annotation { "Feature Type Name" : "Feature", "Feature Type Description" : "" }
export const myFeature = defineFeature(function(context is Context, id is Id, definition is map)
    precondition{}
    {
        {
            var Q0;
            Q0=qCreatedBy(makeId("Top.planeOp"),FACE);
            var sketch = newSketch(context, id + "F0", { "sketchPlane" : qUnion([Q0])});
            skLineSegment(sketch, "E0.bottom", {"start": v(-40.55, -23.12) * mm, "end": v(-42.05, -23.12) * mm});
            skLineSegment(sketch, "E0.top", {"start": v(-40.55, 23.88) * mm, "end": v(-42.05, 23.88) * mm});
            skLineSegment(sketch, "E0.left", {"start": v(-40.55, -23.12) * mm, "end": v(-40.55, 23.88) * mm});
            skLineSegment(sketch, "E0.right", {"start": v(-42.05, -23.12) * mm, "end": v(-42.05, 23.88) * mm});
            skLineSegment(sketch, "E1.bottom", {"start": v(40.45, -23.12) * mm, "end": v(41.95, -23.12) * mm});
            skLineSegment(sketch, "E1.top", {"start": v(40.45, 23.88) * mm, "end": v(41.95, 23.88) * mm});
            skLineSegment(sketch, "E1.left", {"start": v(40.45, -23.12) * mm, "end": v(40.45, 23.88) * mm});
            skLineSegment(sketch, "E1.right", {"start": v(41.95, -23.12) * mm, "end": v(41.95, 23.88) * mm});
            skLineSegment(sketch, "E2.bottom", {"start": v(41.95, 23.88) * mm, "end": v(-42.05, 23.88) * mm});
            skLineSegment(sketch, "E2.top", {"start": v(41.95, 25.38) * mm, "end": v(-42.05, 25.38) * mm});
            skLineSegment(sketch, "E2.left", {"start": v(41.95, 23.88) * mm, "end": v(41.95, 25.38) * mm});
            skLineSegment(sketch, "E2.right", {"start": v(-42.05, 23.88) * mm, "end": v(-42.05, 25.38) * mm});
            skLineSegment(sketch, "E3.bottom", {"start": v(-40.55, -14.22) * mm, "end": v(-35.55, -14.22) * mm});
            skLineSegment(sketch, "E3.top", {"start": v(-40.55, -15.72) * mm, "end": v(-35.55, -15.72) * mm});
            skLineSegment(sketch, "E3.left", {"start": v(-40.55, -14.22) * mm, "end": v(-40.55, -15.72) * mm});
            skLineSegment(sketch, "E3.right", {"start": v(-35.55, -14.22) * mm, "end": v(-35.55, -15.72) * mm});
            skLineSegment(sketch, "E4.bottom", {"start": v(35.45, -15.72) * mm, "end": v(40.45, -15.72) * mm});
            skLineSegment(sketch, "E4.top", {"start": v(35.45, -14.22) * mm, "end": v(40.45, -14.22) * mm});
            skLineSegment(sketch, "E4.left", {"start": v(35.45, -15.72) * mm, "end": v(35.45, -14.22) * mm});
            skLineSegment(sketch, "E4.right", {"start": v(40.45, -15.72) * mm, "end": v(40.45, -14.22) * mm});
            skLineSegment(sketch, "E5.bottom", {"start": v(-41.7, -22.32) * mm, "end": v(-40.9, -22.32) * mm});
            skLineSegment(sketch, "E5.top", {"start": v(-41.7, -18.82) * mm, "end": v(-40.9, -18.82) * mm});
            skLineSegment(sketch, "E5.left", {"start": v(-41.7, -22.32) * mm, "end": v(-41.7, -18.82) * mm});
            skLineSegment(sketch, "E5.right", {"start": v(-40.9, -22.32) * mm, "end": v(-40.9, -18.82) * mm});
            skLineSegment(sketch, "E6.bottom", {"start": v(-41.7, 24.58) * mm, "end": v(-40.9, 24.58) * mm});
            skLineSegment(sketch, "E6.top", {"start": v(-41.7, 21.08) * mm, "end": v(-40.9, 21.08) * mm});
            skLineSegment(sketch, "E6.left", {"start": v(-41.7, 24.58) * mm, "end": v(-41.7, 21.08) * mm});
            skLineSegment(sketch, "E6.right", {"start": v(-40.9, 24.58) * mm, "end": v(-40.9, 21.08) * mm});
            skLineSegment(sketch, "E7.bottom", {"start": v(40.8, 24.58) * mm, "end": v(41.6, 24.58) * mm});
            skLineSegment(sketch, "E7.top", {"start": v(40.8, 21.08) * mm, "end": v(41.6, 21.08) * mm});
            skLineSegment(sketch, "E7.left", {"start": v(40.8, 24.58) * mm, "end": v(40.8, 21.08) * mm});
            skLineSegment(sketch, "E7.right", {"start": v(41.6, 24.58) * mm, "end": v(41.6, 21.08) * mm});
            skLineSegment(sketch, "E8.bottom", {"start": v(40.8, -18.82) * mm, "end": v(41.6, -18.82) * mm});
            skLineSegment(sketch, "E8.top", {"start": v(40.8, -22.32) * mm, "end": v(41.6, -22.32) * mm});
            skLineSegment(sketch, "E8.left", {"start": v(40.8, -18.82) * mm, "end": v(40.8, -22.32) * mm});
            skLineSegment(sketch, "E8.right", {"start": v(41.6, -18.82) * mm, "end": v(41.6, -22.32) * mm});
            skLineSegment(sketch, "E9.bottom", {"start": v(-41.6, -18.92) * mm, "end": v(-41, -18.92) * mm});
            skLineSegment(sketch, "E9.top", {"start": v(-41.6, -22.22) * mm, "end": v(-41, -22.22) * mm});
            skLineSegment(sketch, "E9.left", {"start": v(-41.6, -18.92) * mm, "end": v(-41.6, -22.22) * mm});
            skLineSegment(sketch, "E9.right", {"start": v(-41, -18.92) * mm, "end": v(-41, -22.22) * mm});
            skLineSegment(sketch, "E10.bottom", {"start": v(-41.6, 24.48) * mm, "end": v(-41, 24.48) * mm});
            skLineSegment(sketch, "E10.top", {"start": v(-41.6, 21.18) * mm, "end": v(-41, 21.18) * mm});
            skLineSegment(sketch, "E10.left", {"start": v(-41.6, 24.48) * mm, "end": v(-41.6, 21.18) * mm});
            skLineSegment(sketch, "E10.right", {"start": v(-41, 24.48) * mm, "end": v(-41, 21.18) * mm});
            skLineSegment(sketch, "E11.bottom", {"start": v(40.9, 24.48) * mm, "end": v(41.5, 24.48) * mm});
            skLineSegment(sketch, "E11.top", {"start": v(40.9, 21.18) * mm, "end": v(41.5, 21.18) * mm});
            skLineSegment(sketch, "E11.left", {"start": v(40.9, 24.48) * mm, "end": v(40.9, 21.18) * mm});
            skLineSegment(sketch, "E11.right", {"start": v(41.5, 24.48) * mm, "end": v(41.5, 21.18) * mm});
            skLineSegment(sketch, "E12.bottom", {"start": v(40.9, -18.92) * mm, "end": v(41.5, -18.92) * mm});
            skLineSegment(sketch, "E12.top", {"start": v(40.9, -22.22) * mm, "end": v(41.5, -22.22) * mm});
            skLineSegment(sketch, "E12.left", {"start": v(40.9, -18.92) * mm, "end": v(40.9, -22.22) * mm});
            skLineSegment(sketch, "E12.right", {"start": v(41.5, -18.92) * mm, "end": v(41.5, -22.22) * mm});
            skSolve(sketch);
        }
        {
            var Q0;
            Q0=makeQuery(id+"F0.imprint","IMPRINT",FACE,{"disambiguationData":[TD([[makeQuery(id+"F0.imprint","IMPRINT",EDGE,{"derivedFrom":sQuery(id+"F0.wireOp",EDGE,"E3.bottom")}),-1.0]])]});
            var Q1;
            {var subQ5=sQuery(id+"F0.wireOp",EDGE,"E0.bottom");Q1=makeQuery(id+"F0.imprint","IMPRINT",FACE,{"disambiguationData":[TD([[makeQuery(id+"F0.imprint","IMPRINT",EDGE,{"derivedFrom":subQ5}),-1.0]])]});}
            var Q2;
            Q2=makeQuery(id+"F0.imprint","IMPRINT",FACE,{"disambiguationData":[TD([[makeQuery(id+"F0.imprint","IMPRINT",EDGE,{"derivedFrom":sQuery(id+"F0.wireOp",EDGE,"E2.top")}),1.0]])]});
            var Q3;
            {var subQ5=sQuery(id+"F0.wireOp",EDGE,"E1.bottom");Q3=makeQuery(id+"F0.imprint","IMPRINT",FACE,{"disambiguationData":[TD([[makeQuery(id+"F0.imprint","IMPRINT",EDGE,{"derivedFrom":subQ5}),1.0]])]});}
            var Q4;
            Q4=makeQuery(id+"F0.imprint","IMPRINT",FACE,{"disambiguationData":[TD([[makeQuery(id+"F0.imprint","IMPRINT",EDGE,{"derivedFrom":sQuery(id+"F0.wireOp",EDGE,"E4.bottom")}),1.0]])]});
            var Q5;
            Q5=makeQuery(id+"F0.imprint","IMPRINT",FACE,{"disambiguationData":[TD([[makeQuery(id+"F0.imprint","IMPRINT",EDGE,{"derivedFrom":sQuery(id+"F0.wireOp",EDGE,"E5.bottom")}),1.0]])]});
            var Q6;
            Q6=makeQuery(id+"F0.imprint","IMPRINT",FACE,{"disambiguationData":[TD([[makeQuery(id+"F0.imprint","IMPRINT",EDGE,{"derivedFrom":sQuery(id+"F0.wireOp",EDGE,"E8.bottom")}),-1.0]])]});
            var Q7;
            {var subQ5=sQuery(id+"F0.wireOp",EDGE,"E7.top");Q7=makeQuery(id+"F0.imprint","IMPRINT",FACE,{"disambiguationData":[TD([[makeQuery(id+"F0.imprint","IMPRINT",EDGE,{"derivedFrom":subQ5}),1.0]])]});}
            var Q8;
            {var subQ5=sQuery(id+"F0.wireOp",EDGE,"E7.bottom");Q8=makeQuery(id+"F0.imprint","IMPRINT",FACE,{"disambiguationData":[TD([[makeQuery(id+"F0.imprint","IMPRINT",EDGE,{"derivedFrom":subQ5}),-1.0]])]});}
            var Q9;
            {var subQ5=sQuery(id+"F0.wireOp",EDGE,"E6.bottom");Q9=makeQuery(id+"F0.imprint","IMPRINT",FACE,{"disambiguationData":[TD([[makeQuery(id+"F0.imprint","IMPRINT",EDGE,{"derivedFrom":subQ5}),-1.0]])]});}
            var Q10;
            {var subQ5=sQuery(id+"F0.wireOp",EDGE,"E6.top");Q10=makeQuery(id+"F0.imprint","IMPRINT",FACE,{"disambiguationData":[TD([[makeQuery(id+"F0.imprint","IMPRINT",EDGE,{"derivedFrom":subQ5}),1.0]])]});}
            var Q11;
            Q11=makeQuery(id+"F0.imprint","IMPRINT",FACE,{"disambiguationData":[TD([[makeQuery(id+"F0.imprint","IMPRINT",EDGE,{"derivedFrom":sQuery(id+"F0.wireOp",EDGE,"E9.bottom")}),-1.0]])]});
            var Q12;
            {var subQ5=sQuery(id+"F0.wireOp",EDGE,"E10.top");Q12=makeQuery(id+"F0.imprint","IMPRINT",FACE,{"disambiguationData":[TD([[makeQuery(id+"F0.imprint","IMPRINT",EDGE,{"derivedFrom":subQ5}),1.0]])]});}
            var Q13;
            Q13=makeQuery(id+"F0.imprint","IMPRINT",FACE,{"disambiguationData":[TD([[makeQuery(id+"F0.imprint","IMPRINT",EDGE,{"derivedFrom":sQuery(id+"F0.wireOp",EDGE,"E12.bottom")}),-1.0]])]});
            var Q14;
            {var subQ5=sQuery(id+"F0.wireOp",EDGE,"E11.top");Q14=makeQuery(id+"F0.imprint","IMPRINT",FACE,{"disambiguationData":[TD([[makeQuery(id+"F0.imprint","IMPRINT",EDGE,{"derivedFrom":subQ5}),1.0]])]});}
            var Q15;
            {var subQ5=sQuery(id+"F0.wireOp",EDGE,"E11.bottom");Q15=makeQuery(id+"F0.imprint","IMPRINT",FACE,{"disambiguationData":[TD([[makeQuery(id+"F0.imprint","IMPRINT",EDGE,{"derivedFrom":subQ5}),-1.0]])]});}
            var Q16;
            {var subQ5=sQuery(id+"F0.wireOp",EDGE,"E10.bottom");Q16=makeQuery(id+"F0.imprint","IMPRINT",FACE,{"disambiguationData":[TD([[makeQuery(id+"F0.imprint","IMPRINT",EDGE,{"derivedFrom":subQ5}),-1.0]])]});}
            extrude(context, id + "F1", {"entities" : qUnion([Q0, Q1, Q2, Q3, Q4, Q5, Q6, Q7, Q8, Q9, Q10, Q11, Q12, Q13, Q14, Q15, Q16]), "depth" : 120 * mm, "offsetDistance" : 25 * mm, "hasSecondDirection" : true, "secondDirectionOppositeDirection" : true, "secondDirectionDepth" : 1.5 * mm});
        }
        {
            var Q0;
            Q0=makeQuery(id+"F1.opExtrude","SWEPT_FACE",FACE,{"disambiguationData":[OSD([sQuery(id+"F0.wireOp",EDGE,"E3.top")])]});
            var sketch = newSketch(context, id + "F2", { "sketchPlane" : qUnion([Q0])});
            skPoint(sketch, "E13", {"position": v(-37.51, 4) * mm});
            skPoint(sketch, "E14", {"position": v(-37.51, 2) * mm});
            skPoint(sketch, "E15", {"position": v(-37.48, 11.5) * mm});
            skPoint(sketch, "E16", {"position": v(-37.51, 9.5) * mm});
            skPoint(sketch, "E17", {"position": v(-37.48, 19) * mm});
            skPoint(sketch, "E18", {"position": v(-37.48, 17) * mm});
            skPoint(sketch, "E19", {"position": v(-37.44, 26.5) * mm});
            skPoint(sketch, "E20", {"position": v(-37.44, 24.5) * mm});
            skPoint(sketch, "E21", {"position": v(-37.44, 34) * mm});
            skPoint(sketch, "E22", {"position": v(-37.44, 32) * mm});
            skPoint(sketch, "E23", {"position": v(-37.4, 41.5) * mm});
            skPoint(sketch, "E24", {"position": v(-37.4, 39.5) * mm});
            skPoint(sketch, "E25", {"position": v(-37.4, 49) * mm});
            skPoint(sketch, "E26", {"position": v(-37.4, 47) * mm});
            skPoint(sketch, "E27", {"position": v(-37.37, 56.5) * mm});
            skPoint(sketch, "E28", {"position": v(-37.37, 54.5) * mm});
            skPoint(sketch, "E29", {"position": v(-37.37, 64) * mm});
            skPoint(sketch, "E30", {"position": v(-37.37, 62) * mm});
            skPoint(sketch, "E31", {"position": v(-37.33, 71.5) * mm});
            skPoint(sketch, "E32", {"position": v(-37.37, 69.5) * mm});
            skPoint(sketch, "E33", {"position": v(-37.33, 79) * mm});
            skPoint(sketch, "E34", {"position": v(-37.33, 77) * mm});
            skPoint(sketch, "E35", {"position": v(-37.3, 86.5) * mm});
            skPoint(sketch, "E36", {"position": v(-37.3, 84.5) * mm});
            skPoint(sketch, "E37", {"position": v(-37.3, 94) * mm});
            skPoint(sketch, "E38", {"position": v(-37.3, 92) * mm});
            skPoint(sketch, "E39", {"position": v(-37.25, 101.5) * mm});
            skPoint(sketch, "E40", {"position": v(-37.25, 99.5) * mm});
            skPoint(sketch, "E41", {"position": v(-37.25, 109) * mm});
            skPoint(sketch, "E42", {"position": v(-37.25, 107) * mm});
            skPoint(sketch, "E43", {"position": v(-37.22, 116.5) * mm});
            skPoint(sketch, "E44", {"position": v(-37.22, 114.5) * mm});
            skSolve(sketch);
        }
        {
            var Q0;
            Q0=sQuery(id+"F2.wireOp",VERTEX,"E25");
            var Q1;
            Q1=sQuery(id+"F2.wireOp",VERTEX,"E26");
            var Q2;
            Q2=sQuery(id+"F2.wireOp",VERTEX,"E28");
            var Q3;
            Q3=sQuery(id+"F2.wireOp",VERTEX,"E27");
            var Q4;
            Q4=sQuery(id+"F2.wireOp",VERTEX,"E30");
            var Q5;
            Q5=sQuery(id+"F2.wireOp",VERTEX,"E29");
            var Q6;
            Q6=sQuery(id+"F2.wireOp",VERTEX,"E43");
            var Q7;
            Q7=sQuery(id+"F2.wireOp",VERTEX,"E44");
            var Q8;
            Q8=sQuery(id+"F2.wireOp",VERTEX,"E41");
            var Q9;
            Q9=sQuery(id+"F2.wireOp",VERTEX,"E42");
            var Q10;
            Q10=sQuery(id+"F2.wireOp",VERTEX,"E39");
            var Q11;
            Q11=sQuery(id+"F2.wireOp",VERTEX,"E40");
            var Q12;
            Q12=sQuery(id+"F2.wireOp",VERTEX,"E37");
            var Q13;
            Q13=sQuery(id+"F2.wireOp",VERTEX,"E38");
            var Q14;
            Q14=sQuery(id+"F2.wireOp",VERTEX,"E35");
            var Q15;
            Q15=sQuery(id+"F2.wireOp",VERTEX,"E36");
            var Q16;
            Q16=sQuery(id+"F2.wireOp",VERTEX,"E33");
            var Q17;
            Q17=sQuery(id+"F2.wireOp",VERTEX,"E34");
            var Q18;
            Q18=sQuery(id+"F2.wireOp",VERTEX,"E31");
            var Q19;
            Q19=sQuery(id+"F2.wireOp",VERTEX,"E32");
            var Q20;
            Q20=sQuery(id+"F2.wireOp",VERTEX,"E23");
            var Q21;
            Q21=sQuery(id+"F2.wireOp",VERTEX,"E24");
            var Q22;
            Q22=sQuery(id+"F2.wireOp",VERTEX,"E21");
            var Q23;
            Q23=sQuery(id+"F2.wireOp",VERTEX,"E22");
            var Q24;
            Q24=sQuery(id+"F2.wireOp",VERTEX,"E19");
            var Q25;
            Q25=sQuery(id+"F2.wireOp",VERTEX,"E20");
            var Q26;
            Q26=sQuery(id+"F2.wireOp",VERTEX,"E17");
            var Q27;
            Q27=sQuery(id+"F2.wireOp",VERTEX,"E18");
            var Q28;
            Q28=sQuery(id+"F2.wireOp",VERTEX,"E15");
            var Q29;
            Q29=sQuery(id+"F2.wireOp",VERTEX,"E16");
            var Q30;
            Q30=sQuery(id+"F2.wireOp",VERTEX,"E13");
            var Q31;
            Q31=sQuery(id+"F2.wireOp",VERTEX,"E14");
            var Q32;
            Q32=makeQuery(id+"F1.opExtrude","SWEPT_BODY",BODY,{"disambiguationData":[OSD([sQuery(id+"F0.wireOp",EDGE,"E0.bottom"),sQuery(id+"F0.wireOp",EDGE,"E0.left"),sQuery(id+"F0.wireOp",EDGE,"E0.right"),sQuery(id+"F0.wireOp",EDGE,"E1.bottom"),sQuery(id+"F0.wireOp",EDGE,"E1.left"),sQuery(id+"F0.wireOp",EDGE,"E1.right"),sQuery(id+"F0.wireOp",EDGE,"E2.bottom"),sQuery(id+"F0.wireOp",EDGE,"E2.top"),sQuery(id+"F0.wireOp",EDGE,"E2.left"),sQuery(id+"F0.wireOp",EDGE,"E2.right"),sQuery(id+"F0.wireOp",EDGE,"E3.bottom"),sQuery(id+"F0.wireOp",EDGE,"E3.top"),sQuery(id+"F0.wireOp",EDGE,"E3.right"),sQuery(id+"F0.wireOp",EDGE,"E4.bottom"),sQuery(id+"F0.wireOp",EDGE,"E4.top"),sQuery(id+"F0.wireOp",EDGE,"E4.left")])]});
            hole(context, id + "F3", {"style" : HoleStyle.SIMPLE, "endStyle" : HoleEndStyle.BLIND, "holeDiameter" : .8 * mm, "majorDiameter" : 5 * mm, "holeDepth" : 2 * mm, "isTappedThrough" : true, "tappedDepth" : 12 * mm, "tapClearance" : 3, "locations" : qUnion([Q0, Q1, Q2, Q3, Q4, Q5, Q6, Q7, Q8, Q9, Q10, Q11, Q12, Q13, Q14, Q15, Q16, Q17, Q18, Q19, Q20, Q21, Q22, Q23, Q24, Q25, Q26, Q27, Q28, Q29, Q30, Q31]), "scope" : qUnion([Q32])});
        }
        {
            var Q0;
            Q0=makeQuery(id+"F1.opExtrude","SWEPT_FACE",FACE,{"disambiguationData":[OSD([sQuery(id+"F0.wireOp",EDGE,"E4.bottom")])]});
            var sketch = newSketch(context, id + "F4", { "sketchPlane" : qUnion([Q0])});
            skPoint(sketch, "E45", {"position": v(37.47, 4) * mm});
            skPoint(sketch, "E46", {"position": v(37.47, 2) * mm});
            skPoint(sketch, "E47", {"position": v(37.52, 11.5) * mm});
            skPoint(sketch, "E48", {"position": v(37.47, 9.5) * mm});
            skPoint(sketch, "E49", {"position": v(37.52, 19) * mm});
            skPoint(sketch, "E50", {"position": v(37.52, 17) * mm});
            skPoint(sketch, "E51", {"position": v(37.56, 26.5) * mm});
            skPoint(sketch, "E52", {"position": v(37.56, 24.5) * mm});
            skPoint(sketch, "E53", {"position": v(37.56, 34) * mm});
            skPoint(sketch, "E54", {"position": v(37.56, 32) * mm});
            skPoint(sketch, "E55", {"position": v(37.6, 41.5) * mm});
            skPoint(sketch, "E56", {"position": v(37.6, 39.5) * mm});
            skPoint(sketch, "E57", {"position": v(37.6, 49) * mm});
            skPoint(sketch, "E58", {"position": v(37.6, 47) * mm});
            skPoint(sketch, "E59", {"position": v(37.63, 56.5) * mm});
            skPoint(sketch, "E60", {"position": v(37.63, 54.5) * mm});
            skPoint(sketch, "E61", {"position": v(37.63, 64) * mm});
            skPoint(sketch, "E62", {"position": v(37.63, 62) * mm});
            skPoint(sketch, "E63", {"position": v(37.67, 71.5) * mm});
            skPoint(sketch, "E64", {"position": v(37.63, 69.5) * mm});
            skPoint(sketch, "E65", {"position": v(37.67, 79) * mm});
            skPoint(sketch, "E66", {"position": v(37.67, 77) * mm});
            skPoint(sketch, "E67", {"position": v(37.7, 86.5) * mm});
            skPoint(sketch, "E68", {"position": v(37.7, 84.5) * mm});
            skPoint(sketch, "E69", {"position": v(37.7, 94) * mm});
            skPoint(sketch, "E70", {"position": v(37.7, 92) * mm});
            skPoint(sketch, "E71", {"position": v(37.74, 101.5) * mm});
            skPoint(sketch, "E72", {"position": v(37.74, 99.5) * mm});
            skPoint(sketch, "E73", {"position": v(37.74, 109) * mm});
            skPoint(sketch, "E74", {"position": v(37.74, 107) * mm});
            skPoint(sketch, "E75", {"position": v(37.78, 116.5) * mm});
            skPoint(sketch, "E76", {"position": v(37.78, 114.5) * mm});
            skSolve(sketch);
        }
        {
            var Q0;
            Q0=sQuery(id+"F4.wireOp",VERTEX,"E75");
            var Q1;
            Q1=sQuery(id+"F4.wireOp",VERTEX,"E76");
            var Q2;
            Q2=sQuery(id+"F4.wireOp",VERTEX,"E73");
            var Q3;
            Q3=sQuery(id+"F4.wireOp",VERTEX,"E74");
            var Q4;
            Q4=sQuery(id+"F4.wireOp",VERTEX,"E71");
            var Q5;
            Q5=sQuery(id+"F4.wireOp",VERTEX,"E72");
            var Q6;
            Q6=sQuery(id+"F4.wireOp",VERTEX,"E70");
            var Q7;
            Q7=sQuery(id+"F4.wireOp",VERTEX,"E69");
            var Q8;
            Q8=sQuery(id+"F4.wireOp",VERTEX,"E67");
            var Q9;
            Q9=sQuery(id+"F4.wireOp",VERTEX,"E68");
            var Q10;
            Q10=sQuery(id+"F4.wireOp",VERTEX,"E65");
            var Q11;
            Q11=sQuery(id+"F4.wireOp",VERTEX,"E66");
            var Q12;
            Q12=sQuery(id+"F4.wireOp",VERTEX,"E63");
            var Q13;
            Q13=sQuery(id+"F4.wireOp",VERTEX,"E64");
            var Q14;
            Q14=sQuery(id+"F4.wireOp",VERTEX,"E61");
            var Q15;
            Q15=sQuery(id+"F4.wireOp",VERTEX,"E62");
            var Q16;
            Q16=sQuery(id+"F4.wireOp",VERTEX,"E59");
            var Q17;
            Q17=sQuery(id+"F4.wireOp",VERTEX,"E60");
            var Q18;
            Q18=sQuery(id+"F4.wireOp",VERTEX,"E57");
            var Q19;
            Q19=sQuery(id+"F4.wireOp",VERTEX,"E58");
            var Q20;
            Q20=sQuery(id+"F4.wireOp",VERTEX,"E55");
            var Q21;
            Q21=sQuery(id+"F4.wireOp",VERTEX,"E56");
            var Q22;
            Q22=sQuery(id+"F4.wireOp",VERTEX,"E53");
            var Q23;
            Q23=sQuery(id+"F4.wireOp",VERTEX,"E54");
            var Q24;
            Q24=sQuery(id+"F4.wireOp",VERTEX,"E51");
            var Q25;
            Q25=sQuery(id+"F4.wireOp",VERTEX,"E52");
            var Q26;
            Q26=sQuery(id+"F4.wireOp",VERTEX,"E49");
            var Q27;
            Q27=sQuery(id+"F4.wireOp",VERTEX,"E50");
            var Q28;
            Q28=sQuery(id+"F4.wireOp",VERTEX,"E47");
            var Q29;
            Q29=sQuery(id+"F4.wireOp",VERTEX,"E48");
            var Q30;
            Q30=sQuery(id+"F4.wireOp",VERTEX,"E45");
            var Q31;
            Q31=sQuery(id+"F4.wireOp",VERTEX,"E46");
            var Q32;
            Q32=makeQuery(id+"F1.opExtrude","SWEPT_BODY",BODY,{"disambiguationData":[OSD([sQuery(id+"F0.wireOp",EDGE,"E0.bottom"),sQuery(id+"F0.wireOp",EDGE,"E0.left"),sQuery(id+"F0.wireOp",EDGE,"E0.right"),sQuery(id+"F0.wireOp",EDGE,"E1.bottom"),sQuery(id+"F0.wireOp",EDGE,"E1.left"),sQuery(id+"F0.wireOp",EDGE,"E1.right"),sQuery(id+"F0.wireOp",EDGE,"E2.bottom"),sQuery(id+"F0.wireOp",EDGE,"E2.top"),sQuery(id+"F0.wireOp",EDGE,"E2.left"),sQuery(id+"F0.wireOp",EDGE,"E2.right"),sQuery(id+"F0.wireOp",EDGE,"E3.bottom"),sQuery(id+"F0.wireOp",EDGE,"E3.top"),sQuery(id+"F0.wireOp",EDGE,"E3.right"),sQuery(id+"F0.wireOp",EDGE,"E4.bottom"),sQuery(id+"F0.wireOp",EDGE,"E4.top"),sQuery(id+"F0.wireOp",EDGE,"E4.left")])]});
            hole(context, id + "F5", {"style" : HoleStyle.SIMPLE, "endStyle" : HoleEndStyle.BLIND, "holeDiameter" : .8 * mm, "majorDiameter" : 5 * mm, "holeDepth" : 2 * mm, "isTappedThrough" : true, "tappedDepth" : 12 * mm, "tapClearance" : 3, "locations" : qUnion([Q0, Q1, Q2, Q3, Q4, Q5, Q6, Q7, Q8, Q9, Q10, Q11, Q12, Q13, Q14, Q15, Q16, Q17, Q18, Q19, Q20, Q21, Q22, Q23, Q24, Q25, Q26, Q27, Q28, Q29, Q30, Q31]), "scope" : qUnion([Q32])});
        }
        {
            var Q0;
            {var subQ5=sQuery(id+"F0.wireOp",EDGE,"E10.top");Q0=makeQuery(id+"F0.imprint","IMPRINT",FACE,{"disambiguationData":[TD([[makeQuery(id+"F0.imprint","IMPRINT",EDGE,{"derivedFrom":subQ5}),1.0]])]});}
            var Q1;
            {var subQ5=sQuery(id+"F0.wireOp",EDGE,"E10.bottom");Q1=makeQuery(id+"F0.imprint","IMPRINT",FACE,{"disambiguationData":[TD([[makeQuery(id+"F0.imprint","IMPRINT",EDGE,{"derivedFrom":subQ5}),-1.0]])]});}
            var Q2;
            Q2=makeQuery(id+"F0.imprint","IMPRINT",FACE,{"disambiguationData":[TD([[makeQuery(id+"F0.imprint","IMPRINT",EDGE,{"derivedFrom":sQuery(id+"F0.wireOp",EDGE,"E9.bottom")}),-1.0]])]});
            var Q3;
            {var subQ5=sQuery(id+"F0.wireOp",EDGE,"E11.top");Q3=makeQuery(id+"F0.imprint","IMPRINT",FACE,{"disambiguationData":[TD([[makeQuery(id+"F0.imprint","IMPRINT",EDGE,{"derivedFrom":subQ5}),1.0]])]});}
            var Q4;
            {var subQ5=sQuery(id+"F0.wireOp",EDGE,"E11.bottom");Q4=makeQuery(id+"F0.imprint","IMPRINT",FACE,{"disambiguationData":[TD([[makeQuery(id+"F0.imprint","IMPRINT",EDGE,{"derivedFrom":subQ5}),-1.0]])]});}
            var Q5;
            Q5=makeQuery(id+"F0.imprint","IMPRINT",FACE,{"disambiguationData":[TD([[makeQuery(id+"F0.imprint","IMPRINT",EDGE,{"derivedFrom":sQuery(id+"F0.wireOp",EDGE,"E12.bottom")}),-1.0]])]});
            extrude(context, id + "F6", {"entities" : qUnion([Q0, Q1, Q2, Q3, Q4, Q5]), "oppositeDirection" : true, "depth" : 2.8 * mm, "offsetDistance" : 25 * mm});
        }
        {
            var Q0;
            Q0=makeQuery(id+"F0.imprint","IMPRINT",FACE,{"disambiguationData":[TD([[makeQuery(id+"F0.imprint","IMPRINT",EDGE,{"derivedFrom":sQuery(id+"F0.wireOp",EDGE,"E5.bottom")}),1.0]])]});
            var Q1;
            {var subQ5=sQuery(id+"F0.wireOp",EDGE,"E7.bottom");Q1=makeQuery(id+"F0.imprint","IMPRINT",FACE,{"disambiguationData":[TD([[makeQuery(id+"F0.imprint","IMPRINT",EDGE,{"derivedFrom":subQ5}),-1.0]])]});}
            var Q2;
            {var subQ5=sQuery(id+"F0.wireOp",EDGE,"E10.top");Q2=makeQuery(id+"F0.imprint","IMPRINT",FACE,{"disambiguationData":[TD([[makeQuery(id+"F0.imprint","IMPRINT",EDGE,{"derivedFrom":subQ5}),1.0]])]});}
            var Q3;
            {var subQ1=sQuery(id+"F0.wireOp",EDGE,"E6.top");Q3=makeQuery(id+"F0.imprint","IMPRINT",FACE,{"disambiguationData":[TD([[makeQuery(id+"F0.imprint","IMPRINT",EDGE,{"derivedFrom":subQ1}),1.0]])]});}
            var Q4;
            {var subQ5=sQuery(id+"F0.wireOp",EDGE,"E10.bottom");Q4=makeQuery(id+"F0.imprint","IMPRINT",FACE,{"disambiguationData":[TD([[makeQuery(id+"F0.imprint","IMPRINT",EDGE,{"derivedFrom":subQ5}),-1.0]])]});}
            var Q5;
            {var subQ1=sQuery(id+"F0.wireOp",EDGE,"E6.bottom");Q5=makeQuery(id+"F0.imprint","IMPRINT",FACE,{"disambiguationData":[TD([[makeQuery(id+"F0.imprint","IMPRINT",EDGE,{"derivedFrom":subQ1}),-1.0]])]});}
            var Q6;
            Q6=makeQuery(id+"F0.imprint","IMPRINT",FACE,{"disambiguationData":[TD([[makeQuery(id+"F0.imprint","IMPRINT",EDGE,{"derivedFrom":sQuery(id+"F0.wireOp",EDGE,"E9.bottom")}),-1.0]])]});
            var Q7;
            Q7=makeQuery(id+"F0.imprint","IMPRINT",FACE,{"disambiguationData":[TD([[makeQuery(id+"F0.imprint","IMPRINT",EDGE,{"derivedFrom":sQuery(id+"F0.wireOp",EDGE,"E12.bottom")}),-1.0]])]});
            var Q8;
            Q8=makeQuery(id+"F0.imprint","IMPRINT",FACE,{"disambiguationData":[TD([[makeQuery(id+"F0.imprint","IMPRINT",EDGE,{"derivedFrom":sQuery(id+"F0.wireOp",EDGE,"E8.bottom")}),-1.0]])]});
            var Q9;
            {var subQ1=sQuery(id+"F0.wireOp",EDGE,"E7.top");Q9=makeQuery(id+"F0.imprint","IMPRINT",FACE,{"disambiguationData":[TD([[makeQuery(id+"F0.imprint","IMPRINT",EDGE,{"derivedFrom":subQ1}),1.0]])]});}
            var Q10;
            {var subQ5=sQuery(id+"F0.wireOp",EDGE,"E11.top");Q10=makeQuery(id+"F0.imprint","IMPRINT",FACE,{"disambiguationData":[TD([[makeQuery(id+"F0.imprint","IMPRINT",EDGE,{"derivedFrom":subQ5}),1.0]])]});}
            var Q11;
            {var subQ5=sQuery(id+"F0.wireOp",EDGE,"E11.bottom");Q11=makeQuery(id+"F0.imprint","IMPRINT",FACE,{"disambiguationData":[TD([[makeQuery(id+"F0.imprint","IMPRINT",EDGE,{"derivedFrom":subQ5}),-1.0]])]});}
            extrude(context, id + "F7", {"entities" : qUnion([Q0, Q1, Q2, Q3, Q4, Q5, Q6, Q7, Q8, Q9, Q10, Q11]), "operationType" : NewBodyOperationType.REMOVE, "depth" : 120 * mm, "offsetDistance" : 25 * mm, "hasSecondDirection" : true, "secondDirectionOppositeDirection" : false, "secondDirectionDepth" : 118.5 * mm});
        }
        {
            var Q0;
            Q0=makeQuery(id+"F1.opExtrude","SWEPT_FACE",FACE,{"disambiguationData":[OSD([sQuery(id+"F0.wireOp",EDGE,"E2.top")])]});
            var sketch = newSketch(context, id + "F8", { "sketchPlane" : qUnion([Q0])});
            skLineSegment(sketch, "E77.bottom", {"start": v(-29.95, -1.5) * mm, "end": v(30.05, -1.5) * mm});
            skLineSegment(sketch, "E77.top", {"start": v(-24.95, 8.5) * mm, "end": v(25.05, 8.5) * mm});
            skLineSegment(sketch, "E77.left", {"start": v(-29.95, -1.5) * mm, "end": v(-29.95, 3.5) * mm});
            skLineSegment(sketch, "E77.right", {"start": v(30.05, -1.5) * mm, "end": v(30.05, 3.5) * mm});
            skPoint(sketch, "E78.visualSharp", {"position": v(-29.95, 8.5) * mm});
            skArc(sketch, "E78.filletArc", {"start": v(-24.95, 8.5) * mm, "mid": v(-28.5, 7.04) * mm, "end": v(-29.95, 3.5) * mm});
            skPoint(sketch, "E79.visualSharp", {"position": v(30.05, 8.5) * mm});
            skArc(sketch, "E79.filletArc", {"start": v(30.05, 3.5) * mm, "mid": v(28.58, 7.04) * mm, "end": v(25.05, 8.5) * mm});
            skText(sketch, "E80", { "text": "Raspberry Pi Zero", "fontName": "OpenSans-Regular.ttf"});
            skText(sketch, "E81", { "text": "Mini Rack", "fontName": "OpenSans-Regular.ttf"});
            skText(sketch, "E82", { "text": "By Cyron Design", "fontName": "OpenSans-Regular.ttf"});
            skLineSegment(sketch, "E83", {"start": v(-41.95, 115.78) * mm, "end": v(42.05, 115.78) * mm});
            skPoint(sketch, "E84", {"position": v(0.05, 115.78) * mm});
            skLineSegment(sketch, "E85", {"start": v(-7.06, 71.95) * mm, "end": v(-7.1, 71.95) * mm});
            skLineSegment(sketch, "E86", {"start": v(-7.1, 71.95) * mm, "end": v(-7.32, 71.9) * mm});
            skLineSegment(sketch, "E87", {"start": v(-7.32, 71.9) * mm, "end": v(-7.55, 71.77) * mm});
            skLineSegment(sketch, "E88", {"start": v(-7.55, 71.77) * mm, "end": v(-7.6, 71.73) * mm});
            skLineSegment(sketch, "E89", {"start": v(-7.6, 71.73) * mm, "end": v(-7.68, 71.76) * mm});
            skLineSegment(sketch, "E90", {"start": v(-7.68, 71.76) * mm, "end": v(-7.96, 71.84) * mm});
            skLineSegment(sketch, "E91", {"start": v(-7.96, 71.84) * mm, "end": v(-8.3, 71.88) * mm});
            skLineSegment(sketch, "E92", {"start": v(-8.3, 71.88) * mm, "end": v(-8.64, 71.8) * mm});
            skLineSegment(sketch, "E93", {"start": v(-8.64, 71.8) * mm, "end": v(-8.9, 71.66) * mm});
            skLineSegment(sketch, "E94", {"start": v(-8.9, 71.66) * mm, "end": v(-8.97, 71.6) * mm});
            skLineSegment(sketch, "E95", {"start": v(-8.97, 71.6) * mm, "end": v(-9.07, 71.61) * mm});
            skLineSegment(sketch, "E96", {"start": v(-9.07, 71.61) * mm, "end": v(-9.38, 71.62) * mm});
            skLineSegment(sketch, "E97", {"start": v(-9.38, 71.62) * mm, "end": v(-9.66, 71.56) * mm});
            skLineSegment(sketch, "E98", {"start": v(-9.66, 71.56) * mm, "end": v(-9.85, 71.45) * mm});
            skLineSegment(sketch, "E99", {"start": v(-9.85, 71.45) * mm, "end": v(-9.95, 71.35) * mm});
            skLineSegment(sketch, "E100", {"start": v(-9.95, 71.35) * mm, "end": v(-9.98, 71.3) * mm});
            skLineSegment(sketch, "E101", {"start": v(-9.98, 71.3) * mm, "end": v(-10, 71.3) * mm});
            skLineSegment(sketch, "E102", {"start": v(-10, 71.3) * mm, "end": v(-10.07, 71.31) * mm});
            skLineSegment(sketch, "E103", {"start": v(-10.07, 71.31) * mm, "end": v(-10.22, 71.32) * mm});
            skLineSegment(sketch, "E104", {"start": v(-10.22, 71.32) * mm, "end": v(-10.4, 71.32) * mm});
            skLineSegment(sketch, "E105", {"start": v(-10.4, 71.32) * mm, "end": v(-10.62, 71.3) * mm});
            skLineSegment(sketch, "E106", {"start": v(-10.62, 71.3) * mm, "end": v(-10.85, 71.25) * mm});
            skLineSegment(sketch, "E107", {"start": v(-10.85, 71.25) * mm, "end": v(-11.08, 71.17) * mm});
            skLineSegment(sketch, "E108", {"start": v(-11.08, 71.17) * mm, "end": v(-11.29, 71.03) * mm});
            skLineSegment(sketch, "E109", {"start": v(-11.29, 71.03) * mm, "end": v(-11.43, 70.88) * mm});
            skLineSegment(sketch, "E110", {"start": v(-11.43, 70.88) * mm, "end": v(-11.47, 70.82) * mm});
            skLineSegment(sketch, "E111", {"start": v(-11.47, 70.82) * mm, "end": v(-11.56, 70.83) * mm});
            skLineSegment(sketch, "E112", {"start": v(-11.56, 70.83) * mm, "end": v(-11.83, 70.83) * mm});
            skLineSegment(sketch, "E113", {"start": v(-11.83, 70.83) * mm, "end": v(-12.13, 70.77) * mm});
            skLineSegment(sketch, "E114", {"start": v(-12.13, 70.77) * mm, "end": v(-12.36, 70.64) * mm});
            skLineSegment(sketch, "E115", {"start": v(-12.36, 70.64) * mm, "end": v(-12.52, 70.47) * mm});
            skLineSegment(sketch, "E116", {"start": v(-12.52, 70.47) * mm, "end": v(-12.6, 70.26) * mm});
            skLineSegment(sketch, "E117", {"start": v(-12.6, 70.26) * mm, "end": v(-12.64, 70.02) * mm});
            skLineSegment(sketch, "E118", {"start": v(-12.64, 70.02) * mm, "end": v(-12.6, 69.76) * mm});
            skLineSegment(sketch, "E119", {"start": v(-12.6, 69.76) * mm, "end": v(-12.52, 69.56) * mm});
            skLineSegment(sketch, "E120", {"start": v(-12.52, 69.56) * mm, "end": v(-12.48, 69.5) * mm});
            skLineSegment(sketch, "E121", {"start": v(-12.48, 69.5) * mm, "end": v(-12.53, 69.44) * mm});
            skLineSegment(sketch, "E122", {"start": v(-12.53, 69.44) * mm, "end": v(-12.64, 69.25) * mm});
            skLineSegment(sketch, "E123", {"start": v(-12.64, 69.25) * mm, "end": v(-12.72, 68.96) * mm});
            skLineSegment(sketch, "E124", {"start": v(-12.72, 68.96) * mm, "end": v(-12.67, 68.62) * mm});
            skLineSegment(sketch, "E125", {"start": v(-12.67, 68.62) * mm, "end": v(-12.5, 68.3) * mm});
            skLineSegment(sketch, "E126", {"start": v(-12.5, 68.3) * mm, "end": v(-12.42, 68.2) * mm});
            skLineSegment(sketch, "E127", {"start": v(-12.42, 68.2) * mm, "end": v(-12.45, 68.13) * mm});
            skLineSegment(sketch, "E128", {"start": v(-12.45, 68.13) * mm, "end": v(-12.5, 67.92) * mm});
            skLineSegment(sketch, "E129", {"start": v(-12.5, 67.92) * mm, "end": v(-12.47, 67.63) * mm});
            skLineSegment(sketch, "E130", {"start": v(-12.47, 67.63) * mm, "end": v(-12.32, 67.32) * mm});
            skLineSegment(sketch, "E131", {"start": v(-12.32, 67.32) * mm, "end": v(-12.14, 67.06) * mm});
            skLineSegment(sketch, "E132", {"start": v(-12.14, 67.06) * mm, "end": v(-12.07, 66.99) * mm});
            skLineSegment(sketch, "E133", {"start": v(-12.07, 66.99) * mm, "end": v(-12.08, 66.9) * mm});
            skLineSegment(sketch, "E134", {"start": v(-12.08, 66.9) * mm, "end": v(-12.09, 66.64) * mm});
            skLineSegment(sketch, "E135", {"start": v(-12.09, 66.64) * mm, "end": v(-12, 66.34) * mm});
            skLineSegment(sketch, "E136", {"start": v(-12, 66.34) * mm, "end": v(-11.82, 66.08) * mm});
            skLineSegment(sketch, "E137", {"start": v(-11.82, 66.08) * mm, "end": v(-11.63, 65.9) * mm});
            skLineSegment(sketch, "E138", {"start": v(-11.63, 65.9) * mm, "end": v(-11.56, 65.86) * mm});
            skLineSegment(sketch, "E139", {"start": v(-11.56, 65.86) * mm, "end": v(-11.58, 65.74) * mm});
            skLineSegment(sketch, "E140", {"start": v(-11.58, 65.74) * mm, "end": v(-11.5, 65.4) * mm});
            skLineSegment(sketch, "E141", {"start": v(-11.5, 65.4) * mm, "end": v(-11.25, 65.04) * mm});
            skLineSegment(sketch, "E142", {"start": v(-11.25, 65.04) * mm, "end": v(-10.96, 64.79) * mm});
            skLineSegment(sketch, "E143", {"start": v(-10.96, 64.79) * mm, "end": v(-10.78, 64.67) * mm});
            skLineSegment(sketch, "E144", {"start": v(-10.78, 64.67) * mm, "end": v(-10.73, 64.63) * mm});
            skLineSegment(sketch, "E145", {"start": v(-10.73, 64.63) * mm, "end": v(-10.71, 64.56) * mm});
            skLineSegment(sketch, "E146", {"start": v(-10.71, 64.56) * mm, "end": v(-10.64, 64.34) * mm});
            skLineSegment(sketch, "E147", {"start": v(-10.64, 64.34) * mm, "end": v(-10.47, 64.07) * mm});
            skLineSegment(sketch, "E148", {"start": v(-10.47, 64.07) * mm, "end": v(-10.17, 63.83) * mm});
            skLineSegment(sketch, "E149", {"start": v(-10.17, 63.83) * mm, "end": v(-9.8, 63.68) * mm});
            skLineSegment(sketch, "E150", {"start": v(-9.8, 63.68) * mm, "end": v(-9.68, 63.65) * mm});
            skLineSegment(sketch, "E151", {"start": v(-9.68, 63.65) * mm, "end": v(-9.66, 63.55) * mm});
            skLineSegment(sketch, "E152", {"start": v(-9.66, 63.55) * mm, "end": v(-9.52, 63.28) * mm});
            skLineSegment(sketch, "E153", {"start": v(-9.52, 63.28) * mm, "end": v(-9.26, 63.06) * mm});
            skLineSegment(sketch, "E154", {"start": v(-9.26, 63.06) * mm, "end": v(-8.94, 62.92) * mm});
            skLineSegment(sketch, "E155", {"start": v(-8.94, 62.92) * mm, "end": v(-8.68, 62.85) * mm});
            skLineSegment(sketch, "E156", {"start": v(-8.68, 62.85) * mm, "end": v(-8.6, 62.82) * mm});
            skLineSegment(sketch, "E157", {"start": v(-8.6, 62.82) * mm, "end": v(-8.74, 62.74) * mm});
            skLineSegment(sketch, "E158", {"start": v(-8.74, 62.74) * mm, "end": v(-9.16, 62.47) * mm});
            skLineSegment(sketch, "E159", {"start": v(-9.16, 62.47) * mm, "end": v(-9.7, 62.08) * mm});
            skLineSegment(sketch, "E160", {"start": v(-9.7, 62.08) * mm, "end": v(-10.18, 61.62) * mm});
            skLineSegment(sketch, "E161", {"start": v(-10.18, 61.62) * mm, "end": v(-10.6, 61.09) * mm});
            skLineSegment(sketch, "E162", {"start": v(-10.6, 61.09) * mm, "end": v(-10.96, 60.46) * mm});
            skLineSegment(sketch, "E163", {"start": v(-10.96, 60.46) * mm, "end": v(-11.23, 59.73) * mm});
            skLineSegment(sketch, "E164", {"start": v(-11.23, 59.73) * mm, "end": v(-11.4, 58.86) * mm});
            skLineSegment(sketch, "E165", {"start": v(-11.4, 58.86) * mm, "end": v(-11.45, 58.1) * mm});
            skLineSegment(sketch, "E166", {"start": v(-11.45, 58.1) * mm, "end": v(-11.45, 57.86) * mm});
            skLineSegment(sketch, "E167", {"start": v(-11.45, 57.86) * mm, "end": v(-11.68, 57.45) * mm});
            skLineSegment(sketch, "E168", {"start": v(-11.68, 57.45) * mm, "end": v(-11.76, 57.4) * mm});
            skLineSegment(sketch, "E169", {"start": v(-11.76, 57.4) * mm, "end": v(-12, 57.22) * mm});
            skLineSegment(sketch, "E170", {"start": v(-12, 57.22) * mm, "end": v(-12.32, 56.94) * mm});
            skLineSegment(sketch, "E171", {"start": v(-12.32, 56.94) * mm, "end": v(-12.63, 56.62) * mm});
            skLineSegment(sketch, "E172", {"start": v(-12.63, 56.62) * mm, "end": v(-12.9, 56.25) * mm});
            skLineSegment(sketch, "E173", {"start": v(-12.9, 56.25) * mm, "end": v(-13.16, 55.84) * mm});
            skLineSegment(sketch, "E174", {"start": v(-13.16, 55.84) * mm, "end": v(-13.39, 55.4) * mm});
            skLineSegment(sketch, "E175", {"start": v(-13.39, 55.4) * mm, "end": v(-13.57, 54.93) * mm});
            skLineSegment(sketch, "E176", {"start": v(-13.57, 54.93) * mm, "end": v(-13.7, 54.43) * mm});
            skLineSegment(sketch, "E177", {"start": v(-13.7, 54.43) * mm, "end": v(-13.8, 53.92) * mm});
            skLineSegment(sketch, "E178", {"start": v(-13.8, 53.92) * mm, "end": v(-13.83, 53.39) * mm});
            skLineSegment(sketch, "E179", {"start": v(-13.83, 53.39) * mm, "end": v(-13.8, 52.84) * mm});
            skLineSegment(sketch, "E180", {"start": v(-13.8, 52.84) * mm, "end": v(-13.71, 52.3) * mm});
            skLineSegment(sketch, "E181", {"start": v(-13.71, 52.3) * mm, "end": v(-13.54, 51.74) * mm});
            skLineSegment(sketch, "E182", {"start": v(-13.54, 51.74) * mm, "end": v(-13.3, 51.2) * mm});
            skLineSegment(sketch, "E183", {"start": v(-13.3, 51.2) * mm, "end": v(-12.97, 50.65) * mm});
            skLineSegment(sketch, "E184", {"start": v(-12.97, 50.65) * mm, "end": v(-12.66, 50.24) * mm});
            skLineSegment(sketch, "E185", {"start": v(-12.66, 50.24) * mm, "end": v(-12.55, 50.11) * mm});
            skLineSegment(sketch, "E186", {"start": v(-12.55, 50.11) * mm, "end": v(-12.52, 49.96) * mm});
            skLineSegment(sketch, "E187", {"start": v(-12.52, 49.96) * mm, "end": v(-12.4, 49.5) * mm});
            skLineSegment(sketch, "E188", {"start": v(-12.4, 49.5) * mm, "end": v(-12.24, 48.94) * mm});
            skLineSegment(sketch, "E189", {"start": v(-12.24, 48.94) * mm, "end": v(-12.06, 48.42) * mm});
            skLineSegment(sketch, "E190", {"start": v(-12.06, 48.42) * mm, "end": v(-11.92, 48.03) * mm});
            skLineSegment(sketch, "E191", {"start": v(-11.92, 48.03) * mm, "end": v(-11.87, 47.9) * mm});
            skLineSegment(sketch, "E192", {"start": v(-11.87, 47.9) * mm, "end": v(-11.84, 47.66) * mm});
            skLineSegment(sketch, "E193", {"start": v(-11.84, 47.66) * mm, "end": v(-11.65, 46.92) * mm});
            skLineSegment(sketch, "E194", {"start": v(-11.65, 46.92) * mm, "end": v(-11.28, 46.07) * mm});
            skLineSegment(sketch, "E195", {"start": v(-11.28, 46.07) * mm, "end": v(-10.81, 45.35) * mm});
            skLineSegment(sketch, "E196", {"start": v(-10.81, 45.35) * mm, "end": v(-10.3, 44.76) * mm});
            skLineSegment(sketch, "E197", {"start": v(-10.3, 44.76) * mm, "end": v(-9.76, 44.3) * mm});
            skLineSegment(sketch, "E198", {"start": v(-9.76, 44.3) * mm, "end": v(-9.25, 43.95) * mm});
            skLineSegment(sketch, "E199", {"start": v(-9.25, 43.95) * mm, "end": v(-8.82, 43.73) * mm});
            skLineSegment(sketch, "E200", {"start": v(-8.82, 43.73) * mm, "end": v(-8.6, 43.63) * mm});
            skLineSegment(sketch, "E201", {"start": v(-8.6, 43.63) * mm, "end": v(-8.52, 43.61) * mm});
            skLineSegment(sketch, "E202", {"start": v(-8.52, 43.61) * mm, "end": v(-8.34, 43.48) * mm});
            skLineSegment(sketch, "E203", {"start": v(-8.34, 43.48) * mm, "end": v(-7.81, 43.1) * mm});
            skLineSegment(sketch, "E204", {"start": v(-7.81, 43.1) * mm, "end": v(-7.06, 42.62) * mm});
            skLineSegment(sketch, "E205", {"start": v(-7.06, 42.62) * mm, "end": v(-6.24, 42.17) * mm});
            skLineSegment(sketch, "E206", {"start": v(-6.24, 42.17) * mm, "end": v(-5.54, 41.88) * mm});
            skLineSegment(sketch, "E207", {"start": v(-5.54, 41.88) * mm, "end": v(-5.3, 41.8) * mm});
            skLineSegment(sketch, "E208", {"start": v(-5.3, 41.8) * mm, "end": v(-5.09, 41.57) * mm});
            skLineSegment(sketch, "E209", {"start": v(-5.09, 41.57) * mm, "end": v(-4.36, 40.97) * mm});
            skLineSegment(sketch, "E210", {"start": v(-4.36, 40.97) * mm, "end": v(-3.38, 40.43) * mm});
            skLineSegment(sketch, "E211", {"start": v(-3.38, 40.43) * mm, "end": v(-2.38, 40.12) * mm});
            skLineSegment(sketch, "E212", {"start": v(-2.38, 40.12) * mm, "end": v(-1.62, 40.02) * mm});
            skLineSegment(sketch, "E213", {"start": v(-1.62, 40.02) * mm, "end": v(-1.36, 40.02) * mm});
            skLineSegment(sketch, "E214", {"start": v(-1.36, 40.02) * mm, "end": v(-1.35, 40.02) * mm});
            skLineSegment(sketch, "E215", {"start": v(-1.35, 40.02) * mm, "end": v(-1.3, 40.02) * mm});
            skLineSegment(sketch, "E216", {"start": v(-1.3, 40.02) * mm, "end": v(-1.3, 40.02) * mm});
            skLineSegment(sketch, "E217", {"start": v(-1.3, 40.02) * mm, "end": v(-1.05, 40.02) * mm});
            skLineSegment(sketch, "E218", {"start": v(-1.05, 40.02) * mm, "end": v(-0.29, 40.12) * mm});
            skLineSegment(sketch, "E219", {"start": v(-0.29, 40.12) * mm, "end": v(0.71, 40.43) * mm});
            skLineSegment(sketch, "E220", {"start": v(0.71, 40.43) * mm, "end": v(1.7, 40.97) * mm});
            skLineSegment(sketch, "E221", {"start": v(1.7, 40.97) * mm, "end": v(2.43, 41.57) * mm});
            skLineSegment(sketch, "E222", {"start": v(2.43, 41.57) * mm, "end": v(2.64, 41.8) * mm});
            skLineSegment(sketch, "E223", {"start": v(2.64, 41.8) * mm, "end": v(2.88, 41.88) * mm});
            skLineSegment(sketch, "E224", {"start": v(2.88, 41.88) * mm, "end": v(3.57, 42.17) * mm});
            skLineSegment(sketch, "E225", {"start": v(3.57, 42.17) * mm, "end": v(4.4, 42.62) * mm});
            skLineSegment(sketch, "E226", {"start": v(4.4, 42.62) * mm, "end": v(5.15, 43.1) * mm});
            skLineSegment(sketch, "E227", {"start": v(5.15, 43.1) * mm, "end": v(5.68, 43.48) * mm});
            skLineSegment(sketch, "E228", {"start": v(5.68, 43.48) * mm, "end": v(5.85, 43.61) * mm});
            skLineSegment(sketch, "E229", {"start": v(5.85, 43.61) * mm, "end": v(5.93, 43.63) * mm});
            skLineSegment(sketch, "E230", {"start": v(5.93, 43.63) * mm, "end": v(6.16, 43.73) * mm});
            skLineSegment(sketch, "E231", {"start": v(6.16, 43.73) * mm, "end": v(6.59, 43.95) * mm});
            skLineSegment(sketch, "E232", {"start": v(6.59, 43.95) * mm, "end": v(7.1, 44.3) * mm});
            skLineSegment(sketch, "E233", {"start": v(7.1, 44.3) * mm, "end": v(7.63, 44.76) * mm});
            skLineSegment(sketch, "E234", {"start": v(7.63, 44.76) * mm, "end": v(8.15, 45.35) * mm});
            skLineSegment(sketch, "E235", {"start": v(8.15, 45.35) * mm, "end": v(8.62, 46.07) * mm});
            skLineSegment(sketch, "E236", {"start": v(8.62, 46.07) * mm, "end": v(8.98, 46.92) * mm});
            skLineSegment(sketch, "E237", {"start": v(8.98, 46.92) * mm, "end": v(9.17, 47.66) * mm});
            skLineSegment(sketch, "E238", {"start": v(9.17, 47.66) * mm, "end": v(9.2, 47.9) * mm});
            skLineSegment(sketch, "E239", {"start": v(9.2, 47.9) * mm, "end": v(9.25, 48.03) * mm});
            skLineSegment(sketch, "E240", {"start": v(9.25, 48.03) * mm, "end": v(9.4, 48.42) * mm});
            skLineSegment(sketch, "E241", {"start": v(9.4, 48.42) * mm, "end": v(9.58, 48.94) * mm});
            skLineSegment(sketch, "E242", {"start": v(9.58, 48.94) * mm, "end": v(9.74, 49.5) * mm});
            skLineSegment(sketch, "E243", {"start": v(9.74, 49.5) * mm, "end": v(9.86, 49.96) * mm});
            skLineSegment(sketch, "E244", {"start": v(9.86, 49.96) * mm, "end": v(9.88, 50.11) * mm});
            skLineSegment(sketch, "E245", {"start": v(9.88, 50.11) * mm, "end": v(10, 50.24) * mm});
            skLineSegment(sketch, "E246", {"start": v(10, 50.24) * mm, "end": v(10.3, 50.65) * mm});
            skLineSegment(sketch, "E247", {"start": v(10.3, 50.65) * mm, "end": v(10.63, 51.2) * mm});
            skLineSegment(sketch, "E248", {"start": v(10.63, 51.2) * mm, "end": v(10.88, 51.74) * mm});
            skLineSegment(sketch, "E249", {"start": v(10.88, 51.74) * mm, "end": v(11.05, 52.3) * mm});
            skLineSegment(sketch, "E250", {"start": v(11.05, 52.3) * mm, "end": v(11.14, 52.84) * mm});
            skLineSegment(sketch, "E251", {"start": v(11.14, 52.84) * mm, "end": v(11.17, 53.39) * mm});
            skLineSegment(sketch, "E252", {"start": v(11.17, 53.39) * mm, "end": v(11.13, 53.92) * mm});
            skLineSegment(sketch, "E253", {"start": v(11.13, 53.92) * mm, "end": v(11.04, 54.43) * mm});
            skLineSegment(sketch, "E254", {"start": v(11.04, 54.43) * mm, "end": v(10.9, 54.93) * mm});
            skLineSegment(sketch, "E255", {"start": v(10.9, 54.93) * mm, "end": v(10.72, 55.4) * mm});
            skLineSegment(sketch, "E256", {"start": v(10.72, 55.4) * mm, "end": v(10.5, 55.84) * mm});
            skLineSegment(sketch, "E257", {"start": v(10.5, 55.84) * mm, "end": v(10.24, 56.25) * mm});
            skLineSegment(sketch, "E258", {"start": v(10.24, 56.25) * mm, "end": v(9.96, 56.62) * mm});
            skLineSegment(sketch, "E259", {"start": v(9.96, 56.62) * mm, "end": v(9.66, 56.94) * mm});
            skLineSegment(sketch, "E260", {"start": v(9.66, 56.94) * mm, "end": v(9.34, 57.22) * mm});
            skLineSegment(sketch, "E261", {"start": v(9.34, 57.22) * mm, "end": v(9.1, 57.4) * mm});
            skLineSegment(sketch, "E262", {"start": v(9.1, 57.4) * mm, "end": v(9.01, 57.45) * mm});
            skLineSegment(sketch, "E263", {"start": v(9.01, 57.45) * mm, "end": v(8.79, 57.86) * mm});
            skLineSegment(sketch, "E264", {"start": v(8.79, 57.86) * mm, "end": v(8.79, 58.1) * mm});
            skLineSegment(sketch, "E265", {"start": v(8.79, 58.1) * mm, "end": v(8.73, 58.86) * mm});
            skLineSegment(sketch, "E266", {"start": v(8.73, 58.86) * mm, "end": v(8.56, 59.73) * mm});
            skLineSegment(sketch, "E267", {"start": v(8.56, 59.73) * mm, "end": v(8.3, 60.46) * mm});
            skLineSegment(sketch, "E268", {"start": v(8.3, 60.46) * mm, "end": v(7.94, 61.09) * mm});
            skLineSegment(sketch, "E269", {"start": v(7.94, 61.09) * mm, "end": v(7.52, 61.62) * mm});
            skLineSegment(sketch, "E270", {"start": v(7.52, 61.62) * mm, "end": v(7.03, 62.08) * mm});
            skLineSegment(sketch, "E271", {"start": v(7.03, 62.08) * mm, "end": v(6.5, 62.47) * mm});
            skLineSegment(sketch, "E272", {"start": v(6.5, 62.47) * mm, "end": v(6.08, 62.74) * mm});
            skLineSegment(sketch, "E273", {"start": v(6.08, 62.74) * mm, "end": v(5.93, 62.82) * mm});
            skLineSegment(sketch, "E274", {"start": v(5.93, 62.82) * mm, "end": v(6.02, 62.85) * mm});
            skLineSegment(sketch, "E275", {"start": v(6.02, 62.85) * mm, "end": v(6.28, 62.92) * mm});
            skLineSegment(sketch, "E276", {"start": v(6.28, 62.92) * mm, "end": v(6.6, 63.06) * mm});
            skLineSegment(sketch, "E277", {"start": v(6.6, 63.06) * mm, "end": v(6.85, 63.29) * mm});
            skLineSegment(sketch, "E278", {"start": v(6.85, 63.29) * mm, "end": v(7, 63.55) * mm});
            skLineSegment(sketch, "E279", {"start": v(7, 63.55) * mm, "end": v(7.01, 63.65) * mm});
            skLineSegment(sketch, "E280", {"start": v(7.01, 63.65) * mm, "end": v(7.14, 63.68) * mm});
            skLineSegment(sketch, "E281", {"start": v(7.14, 63.68) * mm, "end": v(7.5, 63.83) * mm});
            skLineSegment(sketch, "E282", {"start": v(7.5, 63.83) * mm, "end": v(7.8, 64.07) * mm});
            skLineSegment(sketch, "E283", {"start": v(7.8, 64.07) * mm, "end": v(7.98, 64.34) * mm});
            skLineSegment(sketch, "E284", {"start": v(7.98, 64.34) * mm, "end": v(8.05, 64.56) * mm});
            skLineSegment(sketch, "E285", {"start": v(8.05, 64.56) * mm, "end": v(8.06, 64.63) * mm});
            skLineSegment(sketch, "E286", {"start": v(8.06, 64.63) * mm, "end": v(8.11, 64.67) * mm});
            skLineSegment(sketch, "E287", {"start": v(8.11, 64.67) * mm, "end": v(8.3, 64.79) * mm});
            skLineSegment(sketch, "E288", {"start": v(8.3, 64.79) * mm, "end": v(8.59, 65.04) * mm});
            skLineSegment(sketch, "E289", {"start": v(8.59, 65.04) * mm, "end": v(8.83, 65.4) * mm});
            skLineSegment(sketch, "E290", {"start": v(8.83, 65.4) * mm, "end": v(8.91, 65.74) * mm});
            skLineSegment(sketch, "E291", {"start": v(8.91, 65.74) * mm, "end": v(8.9, 65.86) * mm});
            skLineSegment(sketch, "E292", {"start": v(8.9, 65.86) * mm, "end": v(8.97, 65.9) * mm});
            skLineSegment(sketch, "E293", {"start": v(8.97, 65.9) * mm, "end": v(9.16, 66.08) * mm});
            skLineSegment(sketch, "E294", {"start": v(9.16, 66.08) * mm, "end": v(9.34, 66.34) * mm});
            skLineSegment(sketch, "E295", {"start": v(9.34, 66.34) * mm, "end": v(9.42, 66.64) * mm});
            skLineSegment(sketch, "E296", {"start": v(9.42, 66.64) * mm, "end": v(9.42, 66.9) * mm});
            skLineSegment(sketch, "E297", {"start": v(9.42, 66.9) * mm, "end": v(9.4, 66.99) * mm});
            skLineSegment(sketch, "E298", {"start": v(9.4, 66.99) * mm, "end": v(9.47, 67.06) * mm});
            skLineSegment(sketch, "E299", {"start": v(9.47, 67.06) * mm, "end": v(9.66, 67.32) * mm});
            skLineSegment(sketch, "E300", {"start": v(9.66, 67.32) * mm, "end": v(9.8, 67.63) * mm});
            skLineSegment(sketch, "E301", {"start": v(9.8, 67.63) * mm, "end": v(9.83, 67.92) * mm});
            skLineSegment(sketch, "E302", {"start": v(9.83, 67.92) * mm, "end": v(9.79, 68.13) * mm});
            skLineSegment(sketch, "E303", {"start": v(9.79, 68.13) * mm, "end": v(9.75, 68.2) * mm});
            skLineSegment(sketch, "E304", {"start": v(9.75, 68.2) * mm, "end": v(9.83, 68.3) * mm});
            skLineSegment(sketch, "E305", {"start": v(9.83, 68.3) * mm, "end": v(10, 68.62) * mm});
            skLineSegment(sketch, "E306", {"start": v(10, 68.62) * mm, "end": v(10.06, 68.96) * mm});
            skLineSegment(sketch, "E307", {"start": v(10.06, 68.96) * mm, "end": v(9.97, 69.25) * mm});
            skLineSegment(sketch, "E308", {"start": v(9.97, 69.25) * mm, "end": v(9.86, 69.44) * mm});
            skLineSegment(sketch, "E309", {"start": v(9.86, 69.44) * mm, "end": v(9.82, 69.5) * mm});
            skLineSegment(sketch, "E310", {"start": v(9.82, 69.5) * mm, "end": v(9.85, 69.56) * mm});
            skLineSegment(sketch, "E311", {"start": v(9.85, 69.56) * mm, "end": v(9.93, 69.76) * mm});
            skLineSegment(sketch, "E312", {"start": v(9.93, 69.76) * mm, "end": v(9.97, 70.02) * mm});
            skLineSegment(sketch, "E313", {"start": v(9.97, 70.02) * mm, "end": v(9.94, 70.26) * mm});
            skLineSegment(sketch, "E314", {"start": v(9.94, 70.26) * mm, "end": v(9.85, 70.47) * mm});
            skLineSegment(sketch, "E315", {"start": v(9.85, 70.47) * mm, "end": v(9.7, 70.65) * mm});
            skLineSegment(sketch, "E316", {"start": v(9.7, 70.65) * mm, "end": v(9.46, 70.77) * mm});
            skLineSegment(sketch, "E317", {"start": v(9.46, 70.77) * mm, "end": v(9.17, 70.83) * mm});
            skLineSegment(sketch, "E318", {"start": v(9.17, 70.83) * mm, "end": v(8.9, 70.83) * mm});
            skLineSegment(sketch, "E319", {"start": v(8.9, 70.83) * mm, "end": v(8.8, 70.82) * mm});
            skLineSegment(sketch, "E320", {"start": v(8.8, 70.82) * mm, "end": v(8.77, 70.88) * mm});
            skLineSegment(sketch, "E321", {"start": v(8.77, 70.88) * mm, "end": v(8.62, 71.03) * mm});
            skLineSegment(sketch, "E322", {"start": v(8.62, 71.03) * mm, "end": v(8.41, 71.17) * mm});
            skLineSegment(sketch, "E323", {"start": v(8.41, 71.17) * mm, "end": v(8.19, 71.25) * mm});
            skLineSegment(sketch, "E324", {"start": v(8.19, 71.25) * mm, "end": v(7.96, 71.3) * mm});
            skLineSegment(sketch, "E325", {"start": v(7.96, 71.3) * mm, "end": v(7.74, 71.32) * mm});
            skLineSegment(sketch, "E326", {"start": v(7.74, 71.32) * mm, "end": v(7.55, 71.32) * mm});
            skLineSegment(sketch, "E327", {"start": v(7.55, 71.32) * mm, "end": v(7.4, 71.31) * mm});
            skLineSegment(sketch, "E328", {"start": v(7.4, 71.31) * mm, "end": v(7.34, 71.3) * mm});
            skLineSegment(sketch, "E329", {"start": v(7.34, 71.3) * mm, "end": v(7.32, 71.3) * mm});
            skLineSegment(sketch, "E330", {"start": v(7.32, 71.3) * mm, "end": v(7.29, 71.35) * mm});
            skLineSegment(sketch, "E331", {"start": v(7.29, 71.35) * mm, "end": v(7.18, 71.45) * mm});
            skLineSegment(sketch, "E332", {"start": v(7.18, 71.45) * mm, "end": v(7, 71.56) * mm});
            skLineSegment(sketch, "E333", {"start": v(7, 71.56) * mm, "end": v(6.71, 71.62) * mm});
            skLineSegment(sketch, "E334", {"start": v(6.71, 71.62) * mm, "end": v(6.4, 71.61) * mm});
            skLineSegment(sketch, "E335", {"start": v(6.4, 71.61) * mm, "end": v(6.3, 71.6) * mm});
            skLineSegment(sketch, "E336", {"start": v(6.3, 71.6) * mm, "end": v(6.23, 71.66) * mm});
            skLineSegment(sketch, "E337", {"start": v(6.23, 71.66) * mm, "end": v(5.98, 71.8) * mm});
            skLineSegment(sketch, "E338", {"start": v(5.98, 71.8) * mm, "end": v(5.64, 71.88) * mm});
            skLineSegment(sketch, "E339", {"start": v(5.64, 71.88) * mm, "end": v(5.3, 71.84) * mm});
            skLineSegment(sketch, "E340", {"start": v(5.3, 71.84) * mm, "end": v(5.02, 71.76) * mm});
            skLineSegment(sketch, "E341", {"start": v(5.02, 71.76) * mm, "end": v(4.93, 71.73) * mm});
            skLineSegment(sketch, "E342", {"start": v(4.93, 71.73) * mm, "end": v(4.85, 71.8) * mm});
            skLineSegment(sketch, "E343", {"start": v(4.85, 71.8) * mm, "end": v(4.53, 71.93) * mm});
            skLineSegment(sketch, "E344", {"start": v(4.53, 71.93) * mm, "end": v(4.19, 71.93) * mm});
            skLineSegment(sketch, "E345", {"start": v(4.19, 71.93) * mm, "end": v(3.86, 71.8) * mm});
            skLineSegment(sketch, "E346", {"start": v(3.86, 71.8) * mm, "end": v(3.63, 71.7) * mm});
            skLineSegment(sketch, "E347", {"start": v(3.63, 71.7) * mm, "end": v(3.55, 71.68) * mm});
            skLineSegment(sketch, "E348", {"start": v(3.55, 71.68) * mm, "end": v(3.44, 71.71) * mm});
            skLineSegment(sketch, "E349", {"start": v(3.44, 71.71) * mm, "end": v(3.11, 71.76) * mm});
            skLineSegment(sketch, "E350", {"start": v(3.11, 71.76) * mm, "end": v(2.82, 71.7) * mm});
            skLineSegment(sketch, "E351", {"start": v(2.82, 71.7) * mm, "end": v(2.58, 71.59) * mm});
            skLineSegment(sketch, "E352", {"start": v(2.58, 71.59) * mm, "end": v(2.41, 71.5) * mm});
            skLineSegment(sketch, "E353", {"start": v(2.41, 71.5) * mm, "end": v(2.35, 71.47) * mm});
            skLineSegment(sketch, "E354", {"start": v(2.35, 71.47) * mm, "end": v(2.23, 71.5) * mm});
            skLineSegment(sketch, "E355", {"start": v(2.23, 71.5) * mm, "end": v(1.87, 71.5) * mm});
            skLineSegment(sketch, "E356", {"start": v(1.87, 71.5) * mm, "end": v(1.53, 71.39) * mm});
            skLineSegment(sketch, "E357", {"start": v(1.53, 71.39) * mm, "end": v(1.26, 71.18) * mm});
            skLineSegment(sketch, "E358", {"start": v(1.26, 71.18) * mm, "end": v(1.07, 70.98) * mm});
            skLineSegment(sketch, "E359", {"start": v(1.07, 70.98) * mm, "end": v(1, 70.91) * mm});
            skLineSegment(sketch, "E360", {"start": v(1, 70.91) * mm, "end": v(0.58, 70.92) * mm});
            skLineSegment(sketch, "E361", {"start": v(0.58, 70.92) * mm, "end": v(0.47, 70.86) * mm});
            skLineSegment(sketch, "E362", {"start": v(0.47, 70.86) * mm, "end": v(0.18, 70.64) * mm});
            skLineSegment(sketch, "E363", {"start": v(0.18, 70.64) * mm, "end": v(-0.17, 70.3) * mm});
            skLineSegment(sketch, "E364", {"start": v(-0.17, 70.3) * mm, "end": v(-0.48, 69.94) * mm});
            skLineSegment(sketch, "E365", {"start": v(-0.48, 69.94) * mm, "end": v(-0.73, 69.56) * mm});
            skLineSegment(sketch, "E366", {"start": v(-0.73, 69.56) * mm, "end": v(-0.94, 69.18) * mm});
            skLineSegment(sketch, "E367", {"start": v(-0.94, 69.18) * mm, "end": v(-1.11, 68.8) * mm});
            skLineSegment(sketch, "E368", {"start": v(-1.11, 68.8) * mm, "end": v(-1.24, 68.47) * mm});
            skLineSegment(sketch, "E369", {"start": v(-1.24, 68.47) * mm, "end": v(-1.31, 68.25) * mm});
            skLineSegment(sketch, "E370", {"start": v(-1.31, 68.25) * mm, "end": v(-1.33, 68.17) * mm});
            skLineSegment(sketch, "E371", {"start": v(-1.33, 68.17) * mm, "end": v(-1.35, 68.25) * mm});
            skLineSegment(sketch, "E372", {"start": v(-1.35, 68.25) * mm, "end": v(-1.43, 68.47) * mm});
            skLineSegment(sketch, "E373", {"start": v(-1.43, 68.47) * mm, "end": v(-1.56, 68.8) * mm});
            skLineSegment(sketch, "E374", {"start": v(-1.56, 68.8) * mm, "end": v(-1.72, 69.18) * mm});
            skLineSegment(sketch, "E375", {"start": v(-1.72, 69.18) * mm, "end": v(-1.94, 69.56) * mm});
            skLineSegment(sketch, "E376", {"start": v(-1.94, 69.56) * mm, "end": v(-2.19, 69.94) * mm});
            skLineSegment(sketch, "E377", {"start": v(-2.19, 69.94) * mm, "end": v(-2.5, 70.3) * mm});
            skLineSegment(sketch, "E378", {"start": v(-2.5, 70.3) * mm, "end": v(-2.84, 70.64) * mm});
            skLineSegment(sketch, "E379", {"start": v(-2.84, 70.64) * mm, "end": v(-3.14, 70.86) * mm});
            skLineSegment(sketch, "E380", {"start": v(-3.14, 70.86) * mm, "end": v(-3.24, 70.92) * mm});
            skLineSegment(sketch, "E381", {"start": v(-3.24, 70.92) * mm, "end": v(-3.67, 70.91) * mm});
            skLineSegment(sketch, "E382", {"start": v(-3.67, 70.91) * mm, "end": v(-3.73, 70.98) * mm});
            skLineSegment(sketch, "E383", {"start": v(-3.73, 70.98) * mm, "end": v(-3.92, 71.18) * mm});
            skLineSegment(sketch, "E384", {"start": v(-3.92, 71.18) * mm, "end": v(-4.2, 71.39) * mm});
            skLineSegment(sketch, "E385", {"start": v(-4.2, 71.39) * mm, "end": v(-4.54, 71.5) * mm});
            skLineSegment(sketch, "E386", {"start": v(-4.54, 71.5) * mm, "end": v(-4.9, 71.5) * mm});
            skLineSegment(sketch, "E387", {"start": v(-4.9, 71.5) * mm, "end": v(-5.02, 71.47) * mm});
            skLineSegment(sketch, "E388", {"start": v(-5.02, 71.47) * mm, "end": v(-5.08, 71.5) * mm});
            skLineSegment(sketch, "E389", {"start": v(-5.08, 71.5) * mm, "end": v(-5.25, 71.59) * mm});
            skLineSegment(sketch, "E390", {"start": v(-5.25, 71.59) * mm, "end": v(-5.48, 71.7) * mm});
            skLineSegment(sketch, "E391", {"start": v(-5.48, 71.7) * mm, "end": v(-5.78, 71.76) * mm});
            skLineSegment(sketch, "E392", {"start": v(-5.78, 71.76) * mm, "end": v(-6.1, 71.71) * mm});
            skLineSegment(sketch, "E393", {"start": v(-6.1, 71.71) * mm, "end": v(-6.21, 71.68) * mm});
            skLineSegment(sketch, "E394", {"start": v(-6.21, 71.68) * mm, "end": v(-6.26, 71.7) * mm});
            skLineSegment(sketch, "E395", {"start": v(-6.26, 71.7) * mm, "end": v(-6.42, 71.76) * mm});
            skLineSegment(sketch, "E396", {"start": v(-6.42, 71.76) * mm, "end": v(-6.63, 71.85) * mm});
            skLineSegment(sketch, "E397", {"start": v(-6.63, 71.85) * mm, "end": v(-6.84, 71.92) * mm});
            skLineSegment(sketch, "E398", {"start": v(-6.84, 71.92) * mm, "end": v(-7, 71.95) * mm});
            skLineSegment(sketch, "E399", {"start": v(-7, 71.95) * mm, "end": v(-7.07, 71.95) * mm});
            skLineSegment(sketch, "E400", {"start": v(-7.07, 71.95) * mm, "end": v(-7.06, 71.95) * mm});
            skLineSegment(sketch, "E401", {"start": v(-9.34, 68.99) * mm, "end": v(-9.07, 68.85) * mm});
            skLineSegment(sketch, "E402", {"start": v(-9.07, 68.85) * mm, "end": v(-8.26, 68.41) * mm});
            skLineSegment(sketch, "E403", {"start": v(-8.26, 68.41) * mm, "end": v(-7.3, 67.87) * mm});
            skLineSegment(sketch, "E404", {"start": v(-7.3, 67.87) * mm, "end": v(-6.44, 67.35) * mm});
            skLineSegment(sketch, "E405", {"start": v(-6.44, 67.35) * mm, "end": v(-5.69, 66.85) * mm});
            skLineSegment(sketch, "E406", {"start": v(-5.69, 66.85) * mm, "end": v(-5.03, 66.38) * mm});
            skLineSegment(sketch, "E407", {"start": v(-5.03, 66.38) * mm, "end": v(-4.46, 65.93) * mm});
            skLineSegment(sketch, "E408", {"start": v(-4.46, 65.93) * mm, "end": v(-3.98, 65.5) * mm});
            skLineSegment(sketch, "E409", {"start": v(-3.98, 65.5) * mm, "end": v(-3.68, 65.19) * mm});
            skLineSegment(sketch, "E410", {"start": v(-3.68, 65.19) * mm, "end": v(-3.58, 65.08) * mm});
            skLineSegment(sketch, "E411", {"start": v(-3.58, 65.08) * mm, "end": v(-3.62, 64.91) * mm});
            skLineSegment(sketch, "E412", {"start": v(-3.62, 64.91) * mm, "end": v(-3.86, 64.42) * mm});
            skLineSegment(sketch, "E413", {"start": v(-3.86, 64.42) * mm, "end": v(-4.28, 63.92) * mm});
            skLineSegment(sketch, "E414", {"start": v(-4.28, 63.92) * mm, "end": v(-4.82, 63.56) * mm});
            skLineSegment(sketch, "E415", {"start": v(-4.82, 63.56) * mm, "end": v(-5.42, 63.31) * mm});
            skLineSegment(sketch, "E416", {"start": v(-5.42, 63.31) * mm, "end": v(-6.04, 63.16) * mm});
            skLineSegment(sketch, "E417", {"start": v(-6.04, 63.16) * mm, "end": v(-6.64, 63.08) * mm});
            skLineSegment(sketch, "E418", {"start": v(-6.64, 63.08) * mm, "end": v(-7.17, 63.06) * mm});
            skLineSegment(sketch, "E419", {"start": v(-7.17, 63.06) * mm, "end": v(-7.5, 63.06) * mm});
            skLineSegment(sketch, "E420", {"start": v(-7.5, 63.06) * mm, "end": v(-7.6, 63.07) * mm});
            skLineSegment(sketch, "E421", {"start": v(-7.6, 63.07) * mm, "end": v(-7.56, 63.08) * mm});
            skLineSegment(sketch, "E422", {"start": v(-7.56, 63.08) * mm, "end": v(-7.46, 63.14) * mm});
            skLineSegment(sketch, "E423", {"start": v(-7.46, 63.14) * mm, "end": v(-7.34, 63.22) * mm});
            skLineSegment(sketch, "E424", {"start": v(-7.34, 63.22) * mm, "end": v(-7.25, 63.32) * mm});
            skLineSegment(sketch, "E425", {"start": v(-7.25, 63.32) * mm, "end": v(-7.2, 63.4) * mm});
            skLineSegment(sketch, "E426", {"start": v(-7.2, 63.4) * mm, "end": v(-7.19, 63.43) * mm});
            skLineSegment(sketch, "E427", {"start": v(-7.19, 63.43) * mm, "end": v(-7.24, 63.47) * mm});
            skLineSegment(sketch, "E428", {"start": v(-7.24, 63.47) * mm, "end": v(-7.46, 63.5) * mm});
            skLineSegment(sketch, "E429", {"start": v(-7.46, 63.5) * mm, "end": v(-7.89, 63.54) * mm});
            skLineSegment(sketch, "E430", {"start": v(-7.89, 63.54) * mm, "end": v(-8.37, 63.6) * mm});
            skLineSegment(sketch, "E431", {"start": v(-8.37, 63.6) * mm, "end": v(-8.74, 63.72) * mm});
            skLineSegment(sketch, "E432", {"start": v(-8.74, 63.72) * mm, "end": v(-8.85, 63.78) * mm});
            skLineSegment(sketch, "E433", {"start": v(-8.85, 63.78) * mm, "end": v(-8.81, 63.78) * mm});
            skLineSegment(sketch, "E434", {"start": v(-8.81, 63.78) * mm, "end": v(-8.7, 63.81) * mm});
            skLineSegment(sketch, "E435", {"start": v(-8.7, 63.81) * mm, "end": v(-8.58, 63.86) * mm});
            skLineSegment(sketch, "E436", {"start": v(-8.58, 63.86) * mm, "end": v(-8.5, 63.93) * mm});
            skLineSegment(sketch, "E437", {"start": v(-8.5, 63.93) * mm, "end": v(-8.43, 64) * mm});
            skLineSegment(sketch, "E438", {"start": v(-8.43, 64) * mm, "end": v(-8.41, 64.03) * mm});
            skLineSegment(sketch, "E439", {"start": v(-8.41, 64.03) * mm, "end": v(-8.52, 64.07) * mm});
            skLineSegment(sketch, "E440", {"start": v(-8.52, 64.07) * mm, "end": v(-8.83, 64.16) * mm});
            skLineSegment(sketch, "E441", {"start": v(-8.83, 64.16) * mm, "end": v(-9.24, 64.3) * mm});
            skLineSegment(sketch, "E442", {"start": v(-9.24, 64.3) * mm, "end": v(-9.6, 64.46) * mm});
            skLineSegment(sketch, "E443", {"start": v(-9.6, 64.46) * mm, "end": v(-9.84, 64.6) * mm});
            skLineSegment(sketch, "E444", {"start": v(-9.84, 64.6) * mm, "end": v(-9.91, 64.66) * mm});
            skLineSegment(sketch, "E445", {"start": v(-9.91, 64.66) * mm, "end": v(-9.88, 64.65) * mm});
            skLineSegment(sketch, "E446", {"start": v(-9.88, 64.65) * mm, "end": v(-9.77, 64.65) * mm});
            skLineSegment(sketch, "E447", {"start": v(-9.77, 64.65) * mm, "end": v(-9.63, 64.65) * mm});
            skLineSegment(sketch, "E448", {"start": v(-9.63, 64.65) * mm, "end": v(-9.47, 64.7) * mm});
            skLineSegment(sketch, "E449", {"start": v(-9.47, 64.7) * mm, "end": v(-9.34, 64.76) * mm});
            skLineSegment(sketch, "E450", {"start": v(-9.34, 64.76) * mm, "end": v(-9.3, 64.78) * mm});
            skLineSegment(sketch, "E451", {"start": v(-9.3, 64.78) * mm, "end": v(-9.42, 64.85) * mm});
            skLineSegment(sketch, "E452", {"start": v(-9.42, 64.85) * mm, "end": v(-10.05, 65.17) * mm});
            skLineSegment(sketch, "E453", {"start": v(-10.05, 65.17) * mm, "end": v(-10.63, 65.57) * mm});
            skLineSegment(sketch, "E454", {"start": v(-10.63, 65.57) * mm, "end": v(-10.73, 65.67) * mm});
            skLineSegment(sketch, "E455", {"start": v(-10.73, 65.67) * mm, "end": v(-10.69, 65.67) * mm});
            skLineSegment(sketch, "E456", {"start": v(-10.69, 65.67) * mm, "end": v(-10.54, 65.68) * mm});
            skLineSegment(sketch, "E457", {"start": v(-10.54, 65.68) * mm, "end": v(-10.36, 65.69) * mm});
            skLineSegment(sketch, "E458", {"start": v(-10.36, 65.69) * mm, "end": v(-10.22, 65.71) * mm});
            skLineSegment(sketch, "E459", {"start": v(-10.22, 65.71) * mm, "end": v(-10.14, 65.75) * mm});
            skLineSegment(sketch, "E460", {"start": v(-10.14, 65.75) * mm, "end": v(-10.12, 65.77) * mm});
            skLineSegment(sketch, "E461", {"start": v(-10.12, 65.77) * mm, "end": v(-10.24, 65.84) * mm});
            skLineSegment(sketch, "E462", {"start": v(-10.24, 65.84) * mm, "end": v(-10.75, 66.21) * mm});
            skLineSegment(sketch, "E463", {"start": v(-10.75, 66.21) * mm, "end": v(-11.2, 66.62) * mm});
            skLineSegment(sketch, "E464", {"start": v(-11.2, 66.62) * mm, "end": v(-11.27, 66.7) * mm});
            skLineSegment(sketch, "E465", {"start": v(-11.27, 66.7) * mm, "end": v(-11.22, 66.7) * mm});
            skLineSegment(sketch, "E466", {"start": v(-11.22, 66.7) * mm, "end": v(-11.04, 66.69) * mm});
            skLineSegment(sketch, "E467", {"start": v(-11.04, 66.69) * mm, "end": v(-10.87, 66.7) * mm});
            skLineSegment(sketch, "E468", {"start": v(-10.87, 66.7) * mm, "end": v(-10.76, 66.72) * mm});
            skLineSegment(sketch, "E469", {"start": v(-10.76, 66.72) * mm, "end": v(-10.7, 66.75) * mm});
            skLineSegment(sketch, "E470", {"start": v(-10.7, 66.75) * mm, "end": v(-10.68, 66.76) * mm});
            skLineSegment(sketch, "E471", {"start": v(-10.68, 66.76) * mm, "end": v(-10.74, 66.83) * mm});
            skLineSegment(sketch, "E472", {"start": v(-10.74, 66.83) * mm, "end": v(-10.95, 67.02) * mm});
            skLineSegment(sketch, "E473", {"start": v(-10.95, 67.02) * mm, "end": v(-11.22, 67.27) * mm});
            skLineSegment(sketch, "E474", {"start": v(-11.22, 67.27) * mm, "end": v(-11.47, 67.54) * mm});
            skLineSegment(sketch, "E475", {"start": v(-11.47, 67.54) * mm, "end": v(-11.62, 67.76) * mm});
            skLineSegment(sketch, "E476", {"start": v(-11.62, 67.76) * mm, "end": v(-11.66, 67.84) * mm});
            skLineSegment(sketch, "E477", {"start": v(-11.66, 67.84) * mm, "end": v(-11.61, 67.82) * mm});
            skLineSegment(sketch, "E478", {"start": v(-11.61, 67.82) * mm, "end": v(-11.47, 67.78) * mm});
            skLineSegment(sketch, "E479", {"start": v(-11.47, 67.78) * mm, "end": v(-11.29, 67.76) * mm});
            skLineSegment(sketch, "E480", {"start": v(-11.29, 67.76) * mm, "end": v(-11.12, 67.78) * mm});
            skLineSegment(sketch, "E481", {"start": v(-11.12, 67.78) * mm, "end": v(-11, 67.82) * mm});
            skLineSegment(sketch, "E482", {"start": v(-11, 67.82) * mm, "end": v(-10.98, 67.85) * mm});
            skLineSegment(sketch, "E483", {"start": v(-10.98, 67.85) * mm, "end": v(-11, 67.9) * mm});
            skLineSegment(sketch, "E484", {"start": v(-11, 67.9) * mm, "end": v(-11.13, 68.03) * mm});
            skLineSegment(sketch, "E485", {"start": v(-11.13, 68.03) * mm, "end": v(-11.36, 68.23) * mm});
            skLineSegment(sketch, "E486", {"start": v(-11.36, 68.23) * mm, "end": v(-11.63, 68.5) * mm});
            skLineSegment(sketch, "E487", {"start": v(-11.63, 68.5) * mm, "end": v(-11.83, 68.78) * mm});
            skLineSegment(sketch, "E488", {"start": v(-11.83, 68.78) * mm, "end": v(-11.88, 68.88) * mm});
            skLineSegment(sketch, "E489", {"start": v(-11.88, 68.88) * mm, "end": v(-11.83, 68.88) * mm});
            skLineSegment(sketch, "E490", {"start": v(-11.83, 68.88) * mm, "end": v(-11.67, 68.86) * mm});
            skLineSegment(sketch, "E491", {"start": v(-11.67, 68.86) * mm, "end": v(-11.48, 68.85) * mm});
            skLineSegment(sketch, "E492", {"start": v(-11.48, 68.85) * mm, "end": v(-11.33, 68.85) * mm});
            skLineSegment(sketch, "E493", {"start": v(-11.33, 68.85) * mm, "end": v(-11.26, 68.87) * mm});
            skLineSegment(sketch, "E494", {"start": v(-11.26, 68.87) * mm, "end": v(-11.24, 68.88) * mm});
            skLineSegment(sketch, "E495", {"start": v(-11.24, 68.88) * mm, "end": v(-11.26, 68.97) * mm});
            skLineSegment(sketch, "E496", {"start": v(-11.26, 68.97) * mm, "end": v(-11.36, 69.24) * mm});
            skLineSegment(sketch, "E497", {"start": v(-11.36, 69.24) * mm, "end": v(-11.5, 69.53) * mm});
            skLineSegment(sketch, "E498", {"start": v(-11.5, 69.53) * mm, "end": v(-11.65, 69.78) * mm});
            skLineSegment(sketch, "E499", {"start": v(-11.65, 69.78) * mm, "end": v(-11.77, 69.96) * mm});
            skLineSegment(sketch, "E500", {"start": v(-11.77, 69.96) * mm, "end": v(-11.81, 70.02) * mm});
            skLineSegment(sketch, "E501", {"start": v(-11.81, 70.02) * mm, "end": v(-11.7, 70.02) * mm});
            skLineSegment(sketch, "E502", {"start": v(-11.7, 70.02) * mm, "end": v(-11.33, 70.02) * mm});
            skLineSegment(sketch, "E503", {"start": v(-11.33, 70.02) * mm, "end": v(-10.84, 70.03) * mm});
            skLineSegment(sketch, "E504", {"start": v(-10.84, 70.03) * mm, "end": v(-10.47, 70.04) * mm});
            skLineSegment(sketch, "E505", {"start": v(-10.47, 70.04) * mm, "end": v(-10.35, 70.07) * mm});
            skLineSegment(sketch, "E506", {"start": v(-10.35, 70.07) * mm, "end": v(-10.72, 70.45) * mm});
            skLineSegment(sketch, "E507", {"start": v(-10.72, 70.45) * mm, "end": v(-10.61, 70.47) * mm});
            skLineSegment(sketch, "E508", {"start": v(-10.61, 70.47) * mm, "end": v(-10.28, 70.5) * mm});
            skLineSegment(sketch, "E509", {"start": v(-10.28, 70.5) * mm, "end": v(-9.85, 70.47) * mm});
            skLineSegment(sketch, "E510", {"start": v(-9.85, 70.47) * mm, "end": v(-9.45, 70.39) * mm});
            skLineSegment(sketch, "E511", {"start": v(-9.45, 70.39) * mm, "end": v(-9.19, 70.31) * mm});
            skLineSegment(sketch, "E512", {"start": v(-9.19, 70.31) * mm, "end": v(-9.1, 70.28) * mm});
            skLineSegment(sketch, "E513", {"start": v(-9.1, 70.28) * mm, "end": v(-9.07, 70.3) * mm});
            skLineSegment(sketch, "E514", {"start": v(-9.07, 70.3) * mm, "end": v(-9.02, 70.4) * mm});
            skLineSegment(sketch, "E515", {"start": v(-9.02, 70.4) * mm, "end": v(-9.06, 70.54) * mm});
            skLineSegment(sketch, "E516", {"start": v(-9.06, 70.54) * mm, "end": v(-9.17, 70.68) * mm});
            skLineSegment(sketch, "E517", {"start": v(-9.17, 70.68) * mm, "end": v(-9.3, 70.8) * mm});
            skLineSegment(sketch, "E518", {"start": v(-9.3, 70.8) * mm, "end": v(-9.34, 70.83) * mm});
            skLineSegment(sketch, "E519", {"start": v(-9.34, 70.83) * mm, "end": v(-9.21, 70.82) * mm});
            skLineSegment(sketch, "E520", {"start": v(-9.21, 70.82) * mm, "end": v(-8.63, 70.7) * mm});
            skLineSegment(sketch, "E521", {"start": v(-8.63, 70.7) * mm, "end": v(-8.09, 70.53) * mm});
            skLineSegment(sketch, "E522", {"start": v(-8.09, 70.53) * mm, "end": v(-7.98, 70.5) * mm});
            skLineSegment(sketch, "E523", {"start": v(-7.98, 70.5) * mm, "end": v(-7.96, 70.52) * mm});
            skLineSegment(sketch, "E524", {"start": v(-7.96, 70.52) * mm, "end": v(-7.92, 70.64) * mm});
            skLineSegment(sketch, "E525", {"start": v(-7.92, 70.64) * mm, "end": v(-8, 70.79) * mm});
            skLineSegment(sketch, "E526", {"start": v(-8, 70.79) * mm, "end": v(-8.15, 70.94) * mm});
            skLineSegment(sketch, "E527", {"start": v(-8.15, 70.94) * mm, "end": v(-8.26, 71.04) * mm});
            skLineSegment(sketch, "E528", {"start": v(-8.26, 71.04) * mm, "end": v(-8.3, 71.08) * mm});
            skLineSegment(sketch, "E529", {"start": v(-8.3, 71.08) * mm, "end": v(-8.17, 71.06) * mm});
            skLineSegment(sketch, "E530", {"start": v(-8.17, 71.06) * mm, "end": v(-7.8, 70.96) * mm});
            skLineSegment(sketch, "E531", {"start": v(-7.8, 70.96) * mm, "end": v(-7.42, 70.83) * mm});
            skLineSegment(sketch, "E532", {"start": v(-7.42, 70.83) * mm, "end": v(-7.13, 70.68) * mm});
            skLineSegment(sketch, "E533", {"start": v(-7.13, 70.68) * mm, "end": v(-6.94, 70.57) * mm});
            skLineSegment(sketch, "E534", {"start": v(-6.94, 70.57) * mm, "end": v(-6.88, 70.53) * mm});
            skLineSegment(sketch, "E535", {"start": v(-6.88, 70.53) * mm, "end": v(-6.85, 70.56) * mm});
            skLineSegment(sketch, "E536", {"start": v(-6.85, 70.56) * mm, "end": v(-6.78, 70.69) * mm});
            skLineSegment(sketch, "E537", {"start": v(-6.78, 70.69) * mm, "end": v(-6.8, 70.84) * mm});
            skLineSegment(sketch, "E538", {"start": v(-6.8, 70.84) * mm, "end": v(-6.9, 71) * mm});
            skLineSegment(sketch, "E539", {"start": v(-6.9, 71) * mm, "end": v(-7, 71.1) * mm});
            skLineSegment(sketch, "E540", {"start": v(-7, 71.1) * mm, "end": v(-7.02, 71.14) * mm});
            skLineSegment(sketch, "E541", {"start": v(-7.02, 71.14) * mm, "end": v(-6.93, 71.1) * mm});
            skLineSegment(sketch, "E542", {"start": v(-6.93, 71.1) * mm, "end": v(-6.64, 70.97) * mm});
            skLineSegment(sketch, "E543", {"start": v(-6.64, 70.97) * mm, "end": v(-6.33, 70.78) * mm});
            skLineSegment(sketch, "E544", {"start": v(-6.33, 70.78) * mm, "end": v(-6.07, 70.58) * mm});
            skLineSegment(sketch, "E545", {"start": v(-6.07, 70.58) * mm, "end": v(-5.9, 70.42) * mm});
            skLineSegment(sketch, "E546", {"start": v(-5.9, 70.42) * mm, "end": v(-5.83, 70.37) * mm});
            skLineSegment(sketch, "E547", {"start": v(-5.83, 70.37) * mm, "end": v(-5.81, 70.4) * mm});
            skLineSegment(sketch, "E548", {"start": v(-5.81, 70.4) * mm, "end": v(-5.75, 70.48) * mm});
            skLineSegment(sketch, "E549", {"start": v(-5.75, 70.48) * mm, "end": v(-5.68, 70.6) * mm});
            skLineSegment(sketch, "E550", {"start": v(-5.68, 70.6) * mm, "end": v(-5.67, 70.75) * mm});
            skLineSegment(sketch, "E551", {"start": v(-5.67, 70.75) * mm, "end": v(-5.73, 70.92) * mm});
            skLineSegment(sketch, "E552", {"start": v(-5.73, 70.92) * mm, "end": v(-5.76, 70.97) * mm});
            skLineSegment(sketch, "E553", {"start": v(-5.76, 70.97) * mm, "end": v(-5.66, 70.91) * mm});
            skLineSegment(sketch, "E554", {"start": v(-5.66, 70.91) * mm, "end": v(-5.21, 70.58) * mm});
            skLineSegment(sketch, "E555", {"start": v(-5.21, 70.58) * mm, "end": v(-4.86, 70.22) * mm});
            skLineSegment(sketch, "E556", {"start": v(-4.86, 70.22) * mm, "end": v(-4.8, 70.14) * mm});
            skLineSegment(sketch, "E557", {"start": v(-4.8, 70.14) * mm, "end": v(-4.77, 70.16) * mm});
            skLineSegment(sketch, "E558", {"start": v(-4.77, 70.16) * mm, "end": v(-4.68, 70.27) * mm});
            skLineSegment(sketch, "E559", {"start": v(-4.68, 70.27) * mm, "end": v(-4.63, 70.42) * mm});
            skLineSegment(sketch, "E560", {"start": v(-4.63, 70.42) * mm, "end": v(-4.64, 70.57) * mm});
            skLineSegment(sketch, "E561", {"start": v(-4.64, 70.57) * mm, "end": v(-4.65, 70.69) * mm});
            skLineSegment(sketch, "E562", {"start": v(-4.65, 70.69) * mm, "end": v(-4.65, 70.73) * mm});
            skLineSegment(sketch, "E563", {"start": v(-4.65, 70.73) * mm, "end": v(-4.55, 70.64) * mm});
            skLineSegment(sketch, "E564", {"start": v(-4.55, 70.64) * mm, "end": v(-4.1, 70.2) * mm});
            skLineSegment(sketch, "E565", {"start": v(-4.1, 70.2) * mm, "end": v(-3.7, 69.74) * mm});
            skLineSegment(sketch, "E566", {"start": v(-3.7, 69.74) * mm, "end": v(-3.62, 69.65) * mm});
            skLineSegment(sketch, "E567", {"start": v(-3.62, 69.65) * mm, "end": v(-3.6, 69.66) * mm});
            skLineSegment(sketch, "E568", {"start": v(-3.6, 69.66) * mm, "end": v(-3.53, 69.8) * mm});
            skLineSegment(sketch, "E569", {"start": v(-3.53, 69.8) * mm, "end": v(-3.46, 70.06) * mm});
            skLineSegment(sketch, "E570", {"start": v(-3.46, 70.06) * mm, "end": v(-3.44, 70.12) * mm});
            skLineSegment(sketch, "E571", {"start": v(-3.44, 70.12) * mm, "end": v(-3.34, 70.02) * mm});
            skLineSegment(sketch, "E572", {"start": v(-3.34, 70.02) * mm, "end": v(-3.05, 69.69) * mm});
            skLineSegment(sketch, "E573", {"start": v(-3.05, 69.69) * mm, "end": v(-2.66, 69.14) * mm});
            skLineSegment(sketch, "E574", {"start": v(-2.66, 69.14) * mm, "end": v(-2.33, 68.53) * mm});
            skLineSegment(sketch, "E575", {"start": v(-2.33, 68.53) * mm, "end": v(-2.1, 67.88) * mm});
            skLineSegment(sketch, "E576", {"start": v(-2.1, 67.88) * mm, "end": v(-2, 67.24) * mm});
            skLineSegment(sketch, "E577", {"start": v(-2, 67.24) * mm, "end": v(-2.1, 66.62) * mm});
            skLineSegment(sketch, "E578", {"start": v(-2.1, 66.62) * mm, "end": v(-2.45, 66.08) * mm});
            skLineSegment(sketch, "E579", {"start": v(-2.45, 66.08) * mm, "end": v(-2.9, 65.73) * mm});
            skLineSegment(sketch, "E580", {"start": v(-2.9, 65.73) * mm, "end": v(-3.07, 65.65) * mm});
            skLineSegment(sketch, "E581", {"start": v(-3.07, 65.65) * mm, "end": v(-3.4, 65.92) * mm});
            skLineSegment(sketch, "E582", {"start": v(-3.4, 65.92) * mm, "end": v(-4.47, 66.68) * mm});
            skLineSegment(sketch, "E583", {"start": v(-4.47, 66.68) * mm, "end": v(-6, 67.57) * mm});
            skLineSegment(sketch, "E584", {"start": v(-6, 67.57) * mm, "end": v(-7.62, 68.33) * mm});
            skLineSegment(sketch, "E585", {"start": v(-7.62, 68.33) * mm, "end": v(-8.9, 68.84) * mm});
            skLineSegment(sketch, "E586", {"start": v(-8.9, 68.84) * mm, "end": v(-9.34, 68.99) * mm});
            skLineSegment(sketch, "E587", {"start": v(6.74, 68.99) * mm, "end": v(6.47, 68.85) * mm});
            skLineSegment(sketch, "E588", {"start": v(6.47, 68.85) * mm, "end": v(5.66, 68.41) * mm});
            skLineSegment(sketch, "E589", {"start": v(5.66, 68.41) * mm, "end": v(4.7, 67.87) * mm});
            skLineSegment(sketch, "E590", {"start": v(4.7, 67.87) * mm, "end": v(3.84, 67.35) * mm});
            skLineSegment(sketch, "E591", {"start": v(3.84, 67.35) * mm, "end": v(3.09, 66.85) * mm});
            skLineSegment(sketch, "E592", {"start": v(3.09, 66.85) * mm, "end": v(2.43, 66.38) * mm});
            skLineSegment(sketch, "E593", {"start": v(2.43, 66.38) * mm, "end": v(1.87, 65.93) * mm});
            skLineSegment(sketch, "E594", {"start": v(1.87, 65.93) * mm, "end": v(1.38, 65.5) * mm});
            skLineSegment(sketch, "E595", {"start": v(1.38, 65.5) * mm, "end": v(1.08, 65.19) * mm});
            skLineSegment(sketch, "E596", {"start": v(1.08, 65.19) * mm, "end": v(0.98, 65.08) * mm});
            skLineSegment(sketch, "E597", {"start": v(0.98, 65.08) * mm, "end": v(1.03, 64.91) * mm});
            skLineSegment(sketch, "E598", {"start": v(1.03, 64.91) * mm, "end": v(1.26, 64.42) * mm});
            skLineSegment(sketch, "E599", {"start": v(1.26, 64.42) * mm, "end": v(1.69, 63.92) * mm});
            skLineSegment(sketch, "E600", {"start": v(1.69, 63.92) * mm, "end": v(2.22, 63.56) * mm});
            skLineSegment(sketch, "E601", {"start": v(2.22, 63.56) * mm, "end": v(2.82, 63.31) * mm});
            skLineSegment(sketch, "E602", {"start": v(2.82, 63.31) * mm, "end": v(3.45, 63.16) * mm});
            skLineSegment(sketch, "E603", {"start": v(3.45, 63.16) * mm, "end": v(4.05, 63.08) * mm});
            skLineSegment(sketch, "E604", {"start": v(4.05, 63.08) * mm, "end": v(4.58, 63.06) * mm});
            skLineSegment(sketch, "E605", {"start": v(4.58, 63.06) * mm, "end": v(4.9, 63.06) * mm});
            skLineSegment(sketch, "E606", {"start": v(4.9, 63.06) * mm, "end": v(5, 63.07) * mm});
            skLineSegment(sketch, "E607", {"start": v(5, 63.07) * mm, "end": v(4.97, 63.08) * mm});
            skLineSegment(sketch, "E608", {"start": v(4.97, 63.08) * mm, "end": v(4.86, 63.14) * mm});
            skLineSegment(sketch, "E609", {"start": v(4.86, 63.14) * mm, "end": v(4.74, 63.22) * mm});
            skLineSegment(sketch, "E610", {"start": v(4.74, 63.22) * mm, "end": v(4.65, 63.32) * mm});
            skLineSegment(sketch, "E611", {"start": v(4.65, 63.32) * mm, "end": v(4.6, 63.4) * mm});
            skLineSegment(sketch, "E612", {"start": v(4.6, 63.4) * mm, "end": v(4.59, 63.43) * mm});
            skLineSegment(sketch, "E613", {"start": v(4.59, 63.43) * mm, "end": v(4.65, 63.47) * mm});
            skLineSegment(sketch, "E614", {"start": v(4.65, 63.47) * mm, "end": v(4.87, 63.5) * mm});
            skLineSegment(sketch, "E615", {"start": v(4.87, 63.5) * mm, "end": v(5.29, 63.54) * mm});
            skLineSegment(sketch, "E616", {"start": v(5.29, 63.54) * mm, "end": v(5.78, 63.6) * mm});
            skLineSegment(sketch, "E617", {"start": v(5.78, 63.6) * mm, "end": v(6.14, 63.72) * mm});
            skLineSegment(sketch, "E618", {"start": v(6.14, 63.72) * mm, "end": v(6.25, 63.78) * mm});
            skLineSegment(sketch, "E619", {"start": v(6.25, 63.78) * mm, "end": v(6.21, 63.78) * mm});
            skLineSegment(sketch, "E620", {"start": v(6.21, 63.78) * mm, "end": v(6.1, 63.81) * mm});
            skLineSegment(sketch, "E621", {"start": v(6.1, 63.81) * mm, "end": v(5.99, 63.86) * mm});
            skLineSegment(sketch, "E622", {"start": v(5.99, 63.86) * mm, "end": v(5.9, 63.93) * mm});
            skLineSegment(sketch, "E623", {"start": v(5.9, 63.93) * mm, "end": v(5.83, 64) * mm});
            skLineSegment(sketch, "E624", {"start": v(5.83, 64) * mm, "end": v(5.82, 64.03) * mm});
            skLineSegment(sketch, "E625", {"start": v(5.82, 64.03) * mm, "end": v(5.92, 64.07) * mm});
            skLineSegment(sketch, "E626", {"start": v(5.92, 64.07) * mm, "end": v(6.23, 64.16) * mm});
            skLineSegment(sketch, "E627", {"start": v(6.23, 64.16) * mm, "end": v(6.64, 64.3) * mm});
            skLineSegment(sketch, "E628", {"start": v(6.64, 64.3) * mm, "end": v(7.01, 64.46) * mm});
            skLineSegment(sketch, "E629", {"start": v(7.01, 64.46) * mm, "end": v(7.25, 64.6) * mm});
            skLineSegment(sketch, "E630", {"start": v(7.25, 64.6) * mm, "end": v(7.32, 64.66) * mm});
            skLineSegment(sketch, "E631", {"start": v(7.32, 64.66) * mm, "end": v(7.28, 64.65) * mm});
            skLineSegment(sketch, "E632", {"start": v(7.28, 64.65) * mm, "end": v(7.17, 64.65) * mm});
            skLineSegment(sketch, "E633", {"start": v(7.17, 64.65) * mm, "end": v(7.03, 64.65) * mm});
            skLineSegment(sketch, "E634", {"start": v(7.03, 64.65) * mm, "end": v(6.88, 64.7) * mm});
            skLineSegment(sketch, "E635", {"start": v(6.88, 64.7) * mm, "end": v(6.74, 64.76) * mm});
            skLineSegment(sketch, "E636", {"start": v(6.74, 64.76) * mm, "end": v(6.7, 64.78) * mm});
            skLineSegment(sketch, "E637", {"start": v(6.7, 64.78) * mm, "end": v(6.83, 64.85) * mm});
            skLineSegment(sketch, "E638", {"start": v(6.83, 64.85) * mm, "end": v(7.45, 65.17) * mm});
            skLineSegment(sketch, "E639", {"start": v(7.45, 65.17) * mm, "end": v(8.04, 65.57) * mm});
            skLineSegment(sketch, "E640", {"start": v(8.04, 65.57) * mm, "end": v(8.14, 65.67) * mm});
            skLineSegment(sketch, "E641", {"start": v(8.14, 65.67) * mm, "end": v(8.1, 65.67) * mm});
            skLineSegment(sketch, "E642", {"start": v(8.1, 65.67) * mm, "end": v(7.95, 65.68) * mm});
            skLineSegment(sketch, "E643", {"start": v(7.95, 65.68) * mm, "end": v(7.77, 65.69) * mm});
            skLineSegment(sketch, "E644", {"start": v(7.77, 65.69) * mm, "end": v(7.62, 65.71) * mm});
            skLineSegment(sketch, "E645", {"start": v(7.62, 65.71) * mm, "end": v(7.54, 65.75) * mm});
            skLineSegment(sketch, "E646", {"start": v(7.54, 65.75) * mm, "end": v(7.53, 65.77) * mm});
            skLineSegment(sketch, "E647", {"start": v(7.53, 65.77) * mm, "end": v(7.64, 65.84) * mm});
            skLineSegment(sketch, "E648", {"start": v(7.64, 65.84) * mm, "end": v(8.15, 66.21) * mm});
            skLineSegment(sketch, "E649", {"start": v(8.15, 66.21) * mm, "end": v(8.6, 66.62) * mm});
            skLineSegment(sketch, "E650", {"start": v(8.6, 66.62) * mm, "end": v(8.68, 66.7) * mm});
            skLineSegment(sketch, "E651", {"start": v(8.68, 66.7) * mm, "end": v(8.62, 66.7) * mm});
            skLineSegment(sketch, "E652", {"start": v(8.62, 66.7) * mm, "end": v(8.45, 66.69) * mm});
            skLineSegment(sketch, "E653", {"start": v(8.45, 66.69) * mm, "end": v(8.28, 66.7) * mm});
            skLineSegment(sketch, "E654", {"start": v(8.28, 66.7) * mm, "end": v(8.16, 66.72) * mm});
            skLineSegment(sketch, "E655", {"start": v(8.16, 66.72) * mm, "end": v(8.1, 66.75) * mm});
            skLineSegment(sketch, "E656", {"start": v(8.1, 66.75) * mm, "end": v(8.08, 66.76) * mm});
            skLineSegment(sketch, "E657", {"start": v(8.08, 66.76) * mm, "end": v(8.15, 66.83) * mm});
            skLineSegment(sketch, "E658", {"start": v(8.15, 66.83) * mm, "end": v(8.35, 67.02) * mm});
            skLineSegment(sketch, "E659", {"start": v(8.35, 67.02) * mm, "end": v(8.62, 67.27) * mm});
            skLineSegment(sketch, "E660", {"start": v(8.62, 67.27) * mm, "end": v(8.87, 67.54) * mm});
            skLineSegment(sketch, "E661", {"start": v(8.87, 67.54) * mm, "end": v(9.03, 67.76) * mm});
            skLineSegment(sketch, "E662", {"start": v(9.03, 67.76) * mm, "end": v(9.07, 67.84) * mm});
            skLineSegment(sketch, "E663", {"start": v(9.07, 67.84) * mm, "end": v(9.02, 67.82) * mm});
            skLineSegment(sketch, "E664", {"start": v(9.02, 67.82) * mm, "end": v(8.87, 67.78) * mm});
            skLineSegment(sketch, "E665", {"start": v(8.87, 67.78) * mm, "end": v(8.69, 67.76) * mm});
            skLineSegment(sketch, "E666", {"start": v(8.69, 67.76) * mm, "end": v(8.52, 67.78) * mm});
            skLineSegment(sketch, "E667", {"start": v(8.52, 67.78) * mm, "end": v(8.41, 67.82) * mm});
            skLineSegment(sketch, "E668", {"start": v(8.41, 67.82) * mm, "end": v(8.38, 67.85) * mm});
            skLineSegment(sketch, "E669", {"start": v(8.38, 67.85) * mm, "end": v(8.4, 67.9) * mm});
            skLineSegment(sketch, "E670", {"start": v(8.4, 67.9) * mm, "end": v(8.53, 68.03) * mm});
            skLineSegment(sketch, "E671", {"start": v(8.53, 68.03) * mm, "end": v(8.77, 68.23) * mm});
            skLineSegment(sketch, "E672", {"start": v(8.77, 68.23) * mm, "end": v(9.04, 68.5) * mm});
            skLineSegment(sketch, "E673", {"start": v(9.04, 68.5) * mm, "end": v(9.24, 68.78) * mm});
            skLineSegment(sketch, "E674", {"start": v(9.24, 68.78) * mm, "end": v(9.28, 68.88) * mm});
            skLineSegment(sketch, "E675", {"start": v(9.28, 68.88) * mm, "end": v(9.23, 68.88) * mm});
            skLineSegment(sketch, "E676", {"start": v(9.23, 68.88) * mm, "end": v(9.07, 68.86) * mm});
            skLineSegment(sketch, "E677", {"start": v(9.07, 68.86) * mm, "end": v(8.88, 68.85) * mm});
            skLineSegment(sketch, "E678", {"start": v(8.88, 68.85) * mm, "end": v(8.73, 68.85) * mm});
            skLineSegment(sketch, "E679", {"start": v(8.73, 68.85) * mm, "end": v(8.66, 68.87) * mm});
            skLineSegment(sketch, "E680", {"start": v(8.66, 68.87) * mm, "end": v(8.65, 68.88) * mm});
            skLineSegment(sketch, "E681", {"start": v(8.65, 68.88) * mm, "end": v(8.67, 68.97) * mm});
            skLineSegment(sketch, "E682", {"start": v(8.67, 68.97) * mm, "end": v(8.76, 69.24) * mm});
            skLineSegment(sketch, "E683", {"start": v(8.76, 69.24) * mm, "end": v(8.9, 69.53) * mm});
            skLineSegment(sketch, "E684", {"start": v(8.9, 69.53) * mm, "end": v(9.06, 69.78) * mm});
            skLineSegment(sketch, "E685", {"start": v(9.06, 69.78) * mm, "end": v(9.18, 69.96) * mm});
            skLineSegment(sketch, "E686", {"start": v(9.18, 69.96) * mm, "end": v(9.22, 70.02) * mm});
            skLineSegment(sketch, "E687", {"start": v(9.22, 70.02) * mm, "end": v(9.1, 70.02) * mm});
            skLineSegment(sketch, "E688", {"start": v(9.1, 70.02) * mm, "end": v(8.73, 70.02) * mm});
            skLineSegment(sketch, "E689", {"start": v(8.73, 70.02) * mm, "end": v(8.24, 70.03) * mm});
            skLineSegment(sketch, "E690", {"start": v(8.24, 70.03) * mm, "end": v(7.88, 70.04) * mm});
            skLineSegment(sketch, "E691", {"start": v(7.88, 70.04) * mm, "end": v(7.75, 70.07) * mm});
            skLineSegment(sketch, "E692", {"start": v(7.75, 70.07) * mm, "end": v(8.12, 70.45) * mm});
            skLineSegment(sketch, "E693", {"start": v(8.12, 70.45) * mm, "end": v(8.02, 70.47) * mm});
            skLineSegment(sketch, "E694", {"start": v(8.02, 70.47) * mm, "end": v(7.68, 70.5) * mm});
            skLineSegment(sketch, "E695", {"start": v(7.68, 70.5) * mm, "end": v(7.25, 70.47) * mm});
            skLineSegment(sketch, "E696", {"start": v(7.25, 70.47) * mm, "end": v(6.86, 70.39) * mm});
            skLineSegment(sketch, "E697", {"start": v(6.86, 70.39) * mm, "end": v(6.59, 70.31) * mm});
            skLineSegment(sketch, "E698", {"start": v(6.59, 70.31) * mm, "end": v(6.5, 70.28) * mm});
            skLineSegment(sketch, "E699", {"start": v(6.5, 70.28) * mm, "end": v(6.47, 70.3) * mm});
            skLineSegment(sketch, "E700", {"start": v(6.47, 70.3) * mm, "end": v(6.42, 70.4) * mm});
            skLineSegment(sketch, "E701", {"start": v(6.42, 70.4) * mm, "end": v(6.46, 70.54) * mm});
            skLineSegment(sketch, "E702", {"start": v(6.46, 70.54) * mm, "end": v(6.58, 70.68) * mm});
            skLineSegment(sketch, "E703", {"start": v(6.58, 70.68) * mm, "end": v(6.7, 70.8) * mm});
            skLineSegment(sketch, "E704", {"start": v(6.7, 70.8) * mm, "end": v(6.74, 70.83) * mm});
            skLineSegment(sketch, "E705", {"start": v(6.74, 70.83) * mm, "end": v(6.62, 70.82) * mm});
            skLineSegment(sketch, "E706", {"start": v(6.62, 70.82) * mm, "end": v(6.03, 70.7) * mm});
            skLineSegment(sketch, "E707", {"start": v(6.03, 70.7) * mm, "end": v(5.49, 70.53) * mm});
            skLineSegment(sketch, "E708", {"start": v(5.49, 70.53) * mm, "end": v(5.39, 70.5) * mm});
            skLineSegment(sketch, "E709", {"start": v(5.39, 70.5) * mm, "end": v(5.36, 70.52) * mm});
            skLineSegment(sketch, "E710", {"start": v(5.36, 70.52) * mm, "end": v(5.32, 70.64) * mm});
            skLineSegment(sketch, "E711", {"start": v(5.32, 70.64) * mm, "end": v(5.4, 70.79) * mm});
            skLineSegment(sketch, "E712", {"start": v(5.4, 70.79) * mm, "end": v(5.55, 70.94) * mm});
            skLineSegment(sketch, "E713", {"start": v(5.55, 70.94) * mm, "end": v(5.67, 71.04) * mm});
            skLineSegment(sketch, "E714", {"start": v(5.67, 71.04) * mm, "end": v(5.7, 71.08) * mm});
            skLineSegment(sketch, "E715", {"start": v(5.7, 71.08) * mm, "end": v(5.58, 71.06) * mm});
            skLineSegment(sketch, "E716", {"start": v(5.58, 71.06) * mm, "end": v(5.2, 70.96) * mm});
            skLineSegment(sketch, "E717", {"start": v(5.2, 70.96) * mm, "end": v(4.83, 70.83) * mm});
            skLineSegment(sketch, "E718", {"start": v(4.83, 70.83) * mm, "end": v(4.53, 70.68) * mm});
            skLineSegment(sketch, "E719", {"start": v(4.53, 70.68) * mm, "end": v(4.35, 70.57) * mm});
            skLineSegment(sketch, "E720", {"start": v(4.35, 70.57) * mm, "end": v(4.28, 70.53) * mm});
            skLineSegment(sketch, "E721", {"start": v(4.28, 70.53) * mm, "end": v(4.25, 70.56) * mm});
            skLineSegment(sketch, "E722", {"start": v(4.25, 70.56) * mm, "end": v(4.18, 70.69) * mm});
            skLineSegment(sketch, "E723", {"start": v(4.18, 70.69) * mm, "end": v(4.2, 70.84) * mm});
            skLineSegment(sketch, "E724", {"start": v(4.2, 70.84) * mm, "end": v(4.3, 71) * mm});
            skLineSegment(sketch, "E725", {"start": v(4.3, 71) * mm, "end": v(4.4, 71.1) * mm});
            skLineSegment(sketch, "E726", {"start": v(4.4, 71.1) * mm, "end": v(4.43, 71.14) * mm});
            skLineSegment(sketch, "E727", {"start": v(4.43, 71.14) * mm, "end": v(4.33, 71.1) * mm});
            skLineSegment(sketch, "E728", {"start": v(4.33, 71.1) * mm, "end": v(4.04, 70.97) * mm});
            skLineSegment(sketch, "E729", {"start": v(4.04, 70.97) * mm, "end": v(3.73, 70.78) * mm});
            skLineSegment(sketch, "E730", {"start": v(3.73, 70.78) * mm, "end": v(3.47, 70.58) * mm});
            skLineSegment(sketch, "E731", {"start": v(3.47, 70.58) * mm, "end": v(3.3, 70.42) * mm});
            skLineSegment(sketch, "E732", {"start": v(3.3, 70.42) * mm, "end": v(3.23, 70.37) * mm});
            skLineSegment(sketch, "E733", {"start": v(3.23, 70.37) * mm, "end": v(3.21, 70.4) * mm});
            skLineSegment(sketch, "E734", {"start": v(3.21, 70.4) * mm, "end": v(3.15, 70.48) * mm});
            skLineSegment(sketch, "E735", {"start": v(3.15, 70.48) * mm, "end": v(3.08, 70.6) * mm});
            skLineSegment(sketch, "E736", {"start": v(3.08, 70.6) * mm, "end": v(3.07, 70.75) * mm});
            skLineSegment(sketch, "E737", {"start": v(3.07, 70.75) * mm, "end": v(3.13, 70.92) * mm});
            skLineSegment(sketch, "E738", {"start": v(3.13, 70.92) * mm, "end": v(3.16, 70.97) * mm});
            skLineSegment(sketch, "E739", {"start": v(3.16, 70.97) * mm, "end": v(3.06, 70.91) * mm});
            skLineSegment(sketch, "E740", {"start": v(3.06, 70.91) * mm, "end": v(2.62, 70.58) * mm});
            skLineSegment(sketch, "E741", {"start": v(2.62, 70.58) * mm, "end": v(2.27, 70.22) * mm});
            skLineSegment(sketch, "E742", {"start": v(2.27, 70.22) * mm, "end": v(2.21, 70.14) * mm});
            skLineSegment(sketch, "E743", {"start": v(2.21, 70.14) * mm, "end": v(2.17, 70.16) * mm});
            skLineSegment(sketch, "E744", {"start": v(2.17, 70.16) * mm, "end": v(2.08, 70.27) * mm});
            skLineSegment(sketch, "E745", {"start": v(2.08, 70.27) * mm, "end": v(2.04, 70.42) * mm});
            skLineSegment(sketch, "E746", {"start": v(2.04, 70.42) * mm, "end": v(2.05, 70.57) * mm});
            skLineSegment(sketch, "E747", {"start": v(2.05, 70.57) * mm, "end": v(2.06, 70.69) * mm});
            skLineSegment(sketch, "E748", {"start": v(2.06, 70.69) * mm, "end": v(2.06, 70.73) * mm});
            skLineSegment(sketch, "E749", {"start": v(2.06, 70.73) * mm, "end": v(1.95, 70.64) * mm});
            skLineSegment(sketch, "E750", {"start": v(1.95, 70.64) * mm, "end": v(1.5, 70.2) * mm});
            skLineSegment(sketch, "E751", {"start": v(1.5, 70.2) * mm, "end": v(1.1, 69.74) * mm});
            skLineSegment(sketch, "E752", {"start": v(1.1, 69.74) * mm, "end": v(1.03, 69.65) * mm});
            skLineSegment(sketch, "E753", {"start": v(1.03, 69.65) * mm, "end": v(1, 69.66) * mm});
            skLineSegment(sketch, "E754", {"start": v(1, 69.66) * mm, "end": v(0.93, 69.8) * mm});
            skLineSegment(sketch, "E755", {"start": v(0.93, 69.8) * mm, "end": v(0.86, 70.06) * mm});
            skLineSegment(sketch, "E756", {"start": v(0.86, 70.06) * mm, "end": v(0.85, 70.12) * mm});
            skLineSegment(sketch, "E757", {"start": v(0.85, 70.12) * mm, "end": v(0.74, 70.02) * mm});
            skLineSegment(sketch, "E758", {"start": v(0.74, 70.02) * mm, "end": v(0.45, 69.69) * mm});
            skLineSegment(sketch, "E759", {"start": v(0.45, 69.69) * mm, "end": v(0.06, 69.14) * mm});
            skLineSegment(sketch, "E760", {"start": v(0.06, 69.14) * mm, "end": v(-0.27, 68.53) * mm});
            skLineSegment(sketch, "E761", {"start": v(-0.27, 68.53) * mm, "end": v(-0.5, 67.88) * mm});
            skLineSegment(sketch, "E762", {"start": v(-0.5, 67.88) * mm, "end": v(-0.6, 67.24) * mm});
            skLineSegment(sketch, "E763", {"start": v(-0.6, 67.24) * mm, "end": v(-0.5, 66.62) * mm});
            skLineSegment(sketch, "E764", {"start": v(-0.5, 66.62) * mm, "end": v(-0.15, 66.08) * mm});
            skLineSegment(sketch, "E765", {"start": v(-0.15, 66.08) * mm, "end": v(0.3, 65.73) * mm});
            skLineSegment(sketch, "E766", {"start": v(0.3, 65.73) * mm, "end": v(0.48, 65.65) * mm});
            skLineSegment(sketch, "E767", {"start": v(0.48, 65.65) * mm, "end": v(0.81, 65.92) * mm});
            skLineSegment(sketch, "E768", {"start": v(0.81, 65.92) * mm, "end": v(1.88, 66.68) * mm});
            skLineSegment(sketch, "E769", {"start": v(1.88, 66.68) * mm, "end": v(3.4, 67.57) * mm});
            skLineSegment(sketch, "E770", {"start": v(3.4, 67.57) * mm, "end": v(5.02, 68.33) * mm});
            skLineSegment(sketch, "E771", {"start": v(5.02, 68.33) * mm, "end": v(6.3, 68.84) * mm});
            skLineSegment(sketch, "E772", {"start": v(6.3, 68.84) * mm, "end": v(6.74, 68.99) * mm});
            skLineSegment(sketch, "E773", {"start": v(2.37, 48.8) * mm, "end": v(2.37, 48.65) * mm});
            skLineSegment(sketch, "E774", {"start": v(2.37, 48.65) * mm, "end": v(2.3, 48.15) * mm});
            skLineSegment(sketch, "E775", {"start": v(2.3, 48.15) * mm, "end": v(2.1, 47.52) * mm});
            skLineSegment(sketch, "E776", {"start": v(2.1, 47.52) * mm, "end": v(1.77, 46.94) * mm});
            skLineSegment(sketch, "E777", {"start": v(1.77, 46.94) * mm, "end": v(1.44, 46.55) * mm});
            skLineSegment(sketch, "E778", {"start": v(1.44, 46.55) * mm, "end": v(1.32, 46.43) * mm});
            skLineSegment(sketch, "E779", {"start": v(1.32, 46.43) * mm, "end": v(1.19, 46.31) * mm});
            skLineSegment(sketch, "E780", {"start": v(1.19, 46.31) * mm, "end": v(0.76, 46.01) * mm});
            skLineSegment(sketch, "E781", {"start": v(0.76, 46.01) * mm, "end": v(0.14, 45.7) * mm});
            skLineSegment(sketch, "E782", {"start": v(0.14, 45.7) * mm, "end": v(-0.54, 45.51) * mm});
            skLineSegment(sketch, "E783", {"start": v(-0.54, 45.51) * mm, "end": v(-1.08, 45.44) * mm});
            skLineSegment(sketch, "E784", {"start": v(-1.08, 45.44) * mm, "end": v(-1.26, 45.44) * mm});
            skLineSegment(sketch, "E785", {"start": v(-1.26, 45.44) * mm, "end": v(-1.44, 45.44) * mm});
            skLineSegment(sketch, "E786", {"start": v(-1.44, 45.44) * mm, "end": v(-1.97, 45.51) * mm});
            skLineSegment(sketch, "E787", {"start": v(-1.97, 45.51) * mm, "end": v(-2.65, 45.7) * mm});
            skLineSegment(sketch, "E788", {"start": v(-2.65, 45.7) * mm, "end": v(-3.28, 46.01) * mm});
            skLineSegment(sketch, "E789", {"start": v(-3.28, 46.01) * mm, "end": v(-3.7, 46.31) * mm});
            skLineSegment(sketch, "E790", {"start": v(-3.7, 46.31) * mm, "end": v(-3.83, 46.43) * mm});
            skLineSegment(sketch, "E791", {"start": v(-3.83, 46.43) * mm, "end": v(-3.96, 46.55) * mm});
            skLineSegment(sketch, "E792", {"start": v(-3.96, 46.55) * mm, "end": v(-4.29, 46.94) * mm});
            skLineSegment(sketch, "E793", {"start": v(-4.29, 46.94) * mm, "end": v(-4.62, 47.52) * mm});
            skLineSegment(sketch, "E794", {"start": v(-4.62, 47.52) * mm, "end": v(-4.82, 48.15) * mm});
            skLineSegment(sketch, "E795", {"start": v(-4.82, 48.15) * mm, "end": v(-4.89, 48.65) * mm});
            skLineSegment(sketch, "E796", {"start": v(-4.89, 48.65) * mm, "end": v(-4.89, 48.8) * mm});
            skLineSegment(sketch, "E797", {"start": v(-4.89, 48.8) * mm, "end": v(-4.89, 48.97) * mm});
            skLineSegment(sketch, "E798", {"start": v(-4.89, 48.97) * mm, "end": v(-4.82, 49.47) * mm});
            skLineSegment(sketch, "E799", {"start": v(-4.82, 49.47) * mm, "end": v(-4.62, 50.1) * mm});
            skLineSegment(sketch, "E800", {"start": v(-4.62, 50.1) * mm, "end": v(-4.29, 50.68) * mm});
            skLineSegment(sketch, "E801", {"start": v(-4.29, 50.68) * mm, "end": v(-3.96, 51.07) * mm});
            skLineSegment(sketch, "E802", {"start": v(-3.96, 51.07) * mm, "end": v(-3.83, 51.19) * mm});
            skLineSegment(sketch, "E803", {"start": v(-3.83, 51.19) * mm, "end": v(-3.7, 51.3) * mm});
            skLineSegment(sketch, "E804", {"start": v(-3.7, 51.3) * mm, "end": v(-3.28, 51.6) * mm});
            skLineSegment(sketch, "E805", {"start": v(-3.28, 51.6) * mm, "end": v(-2.65, 51.92) * mm});
            skLineSegment(sketch, "E806", {"start": v(-2.65, 51.92) * mm, "end": v(-1.97, 52.1) * mm});
            skLineSegment(sketch, "E807", {"start": v(-1.97, 52.1) * mm, "end": v(-1.44, 52.18) * mm});
            skLineSegment(sketch, "E808", {"start": v(-1.44, 52.18) * mm, "end": v(-1.26, 52.18) * mm});
            skLineSegment(sketch, "E809", {"start": v(-1.26, 52.18) * mm, "end": v(-1.08, 52.18) * mm});
            skLineSegment(sketch, "E810", {"start": v(-1.08, 52.18) * mm, "end": v(-0.54, 52.1) * mm});
            skLineSegment(sketch, "E811", {"start": v(-0.54, 52.1) * mm, "end": v(0.14, 51.92) * mm});
            skLineSegment(sketch, "E812", {"start": v(0.14, 51.92) * mm, "end": v(0.76, 51.6) * mm});
            skLineSegment(sketch, "E813", {"start": v(0.76, 51.6) * mm, "end": v(1.19, 51.3) * mm});
            skLineSegment(sketch, "E814", {"start": v(1.19, 51.3) * mm, "end": v(1.32, 51.19) * mm});
            skLineSegment(sketch, "E815", {"start": v(1.32, 51.19) * mm, "end": v(1.44, 51.07) * mm});
            skLineSegment(sketch, "E816", {"start": v(1.44, 51.07) * mm, "end": v(1.77, 50.68) * mm});
            skLineSegment(sketch, "E817", {"start": v(1.77, 50.68) * mm, "end": v(2.1, 50.1) * mm});
            skLineSegment(sketch, "E818", {"start": v(2.1, 50.1) * mm, "end": v(2.3, 49.47) * mm});
            skLineSegment(sketch, "E819", {"start": v(2.3, 49.47) * mm, "end": v(2.37, 48.97) * mm});
            skLineSegment(sketch, "E820", {"start": v(2.37, 48.97) * mm, "end": v(2.37, 48.8) * mm});
            skLineSegment(sketch, "E821", {"start": v(-3.36, 58.37) * mm, "end": v(-3.22, 58.28) * mm});
            skLineSegment(sketch, "E822", {"start": v(-3.22, 58.28) * mm, "end": v(-2.85, 57.95) * mm});
            skLineSegment(sketch, "E823", {"start": v(-2.85, 57.95) * mm, "end": v(-2.47, 57.43) * mm});
            skLineSegment(sketch, "E824", {"start": v(-2.47, 57.43) * mm, "end": v(-2.2, 56.83) * mm});
            skLineSegment(sketch, "E825", {"start": v(-2.2, 56.83) * mm, "end": v(-2.05, 56.17) * mm});
            skLineSegment(sketch, "E826", {"start": v(-2.05, 56.17) * mm, "end": v(-2.03, 55.48) * mm});
            skLineSegment(sketch, "E827", {"start": v(-2.03, 55.48) * mm, "end": v(-2.14, 54.77) * mm});
            skLineSegment(sketch, "E828", {"start": v(-2.14, 54.77) * mm, "end": v(-2.38, 54.07) * mm});
            skLineSegment(sketch, "E829", {"start": v(-2.38, 54.07) * mm, "end": v(-2.65, 53.55) * mm});
            skLineSegment(sketch, "E830", {"start": v(-2.65, 53.55) * mm, "end": v(-2.75, 53.38) * mm});
            skLineSegment(sketch, "E831", {"start": v(-2.75, 53.38) * mm, "end": v(-2.86, 53.22) * mm});
            skLineSegment(sketch, "E832", {"start": v(-2.86, 53.22) * mm, "end": v(-3.24, 52.77) * mm});
            skLineSegment(sketch, "E833", {"start": v(-3.24, 52.77) * mm, "end": v(-3.8, 52.28) * mm});
            skLineSegment(sketch, "E834", {"start": v(-3.8, 52.28) * mm, "end": v(-4.4, 51.9) * mm});
            skLineSegment(sketch, "E835", {"start": v(-4.4, 51.9) * mm, "end": v(-5.05, 51.64) * mm});
            skLineSegment(sketch, "E836", {"start": v(-5.05, 51.64) * mm, "end": v(-5.71, 51.51) * mm});
            skLineSegment(sketch, "E837", {"start": v(-5.71, 51.51) * mm, "end": v(-6.37, 51.52) * mm});
            skLineSegment(sketch, "E838", {"start": v(-6.37, 51.52) * mm, "end": v(-7, 51.67) * mm});
            skLineSegment(sketch, "E839", {"start": v(-7, 51.67) * mm, "end": v(-7.46, 51.87) * mm});
            skLineSegment(sketch, "E840", {"start": v(-7.46, 51.87) * mm, "end": v(-7.6, 51.96) * mm});
            skLineSegment(sketch, "E841", {"start": v(-7.6, 51.96) * mm, "end": v(-7.73, 52.05) * mm});
            skLineSegment(sketch, "E842", {"start": v(-7.73, 52.05) * mm, "end": v(-8.1, 52.39) * mm});
            skLineSegment(sketch, "E843", {"start": v(-8.1, 52.39) * mm, "end": v(-8.49, 52.9) * mm});
            skLineSegment(sketch, "E844", {"start": v(-8.49, 52.9) * mm, "end": v(-8.76, 53.5) * mm});
            skLineSegment(sketch, "E845", {"start": v(-8.76, 53.5) * mm, "end": v(-8.9, 54.16) * mm});
            skLineSegment(sketch, "E846", {"start": v(-8.9, 54.16) * mm, "end": v(-8.92, 54.86) * mm});
            skLineSegment(sketch, "E847", {"start": v(-8.92, 54.86) * mm, "end": v(-8.81, 55.56) * mm});
            skLineSegment(sketch, "E848", {"start": v(-8.81, 55.56) * mm, "end": v(-8.57, 56.27) * mm});
            skLineSegment(sketch, "E849", {"start": v(-8.57, 56.27) * mm, "end": v(-8.3, 56.8) * mm});
            skLineSegment(sketch, "E850", {"start": v(-8.3, 56.8) * mm, "end": v(-8.2, 56.95) * mm});
            skLineSegment(sketch, "E851", {"start": v(-8.2, 56.95) * mm, "end": v(-8.1, 57.11) * mm});
            skLineSegment(sketch, "E852", {"start": v(-8.1, 57.11) * mm, "end": v(-7.72, 57.56) * mm});
            skLineSegment(sketch, "E853", {"start": v(-7.72, 57.56) * mm, "end": v(-7.16, 58.06) * mm});
            skLineSegment(sketch, "E854", {"start": v(-7.16, 58.06) * mm, "end": v(-6.55, 58.44) * mm});
            skLineSegment(sketch, "E855", {"start": v(-6.55, 58.44) * mm, "end": v(-5.9, 58.7) * mm});
            skLineSegment(sketch, "E856", {"start": v(-5.9, 58.7) * mm, "end": v(-5.24, 58.82) * mm});
            skLineSegment(sketch, "E857", {"start": v(-5.24, 58.82) * mm, "end": v(-4.59, 58.82) * mm});
            skLineSegment(sketch, "E858", {"start": v(-4.59, 58.82) * mm, "end": v(-3.95, 58.67) * mm});
            skLineSegment(sketch, "E859", {"start": v(-3.95, 58.67) * mm, "end": v(-3.5, 58.46) * mm});
            skLineSegment(sketch, "E860", {"start": v(-3.5, 58.46) * mm, "end": v(-3.36, 58.37) * mm});
            skLineSegment(sketch, "E861", {"start": v(0.7, 58.55) * mm, "end": v(0.56, 58.46) * mm});
            skLineSegment(sketch, "E862", {"start": v(0.56, 58.46) * mm, "end": v(0.2, 58.13) * mm});
            skLineSegment(sketch, "E863", {"start": v(0.2, 58.13) * mm, "end": v(-0.2, 57.6) * mm});
            skLineSegment(sketch, "E864", {"start": v(-0.2, 57.6) * mm, "end": v(-0.46, 57) * mm});
            skLineSegment(sketch, "E865", {"start": v(-0.46, 57) * mm, "end": v(-0.6, 56.35) * mm});
            skLineSegment(sketch, "E866", {"start": v(-0.6, 56.35) * mm, "end": v(-0.62, 55.66) * mm});
            skLineSegment(sketch, "E867", {"start": v(-0.62, 55.66) * mm, "end": v(-0.52, 54.95) * mm});
            skLineSegment(sketch, "E868", {"start": v(-0.52, 54.95) * mm, "end": v(-0.28, 54.24) * mm});
            skLineSegment(sketch, "E869", {"start": v(-0.28, 54.24) * mm, "end": v(-0.01, 53.72) * mm});
            skLineSegment(sketch, "E870", {"start": v(-0.01, 53.72) * mm, "end": v(0.1, 53.56) * mm});
            skLineSegment(sketch, "E871", {"start": v(0.1, 53.56) * mm, "end": v(0.2, 53.4) * mm});
            skLineSegment(sketch, "E872", {"start": v(0.2, 53.4) * mm, "end": v(0.58, 52.95) * mm});
            skLineSegment(sketch, "E873", {"start": v(0.58, 52.95) * mm, "end": v(1.13, 52.45) * mm});
            skLineSegment(sketch, "E874", {"start": v(1.13, 52.45) * mm, "end": v(1.75, 52.07) * mm});
            skLineSegment(sketch, "E875", {"start": v(1.75, 52.07) * mm, "end": v(2.4, 51.82) * mm});
            skLineSegment(sketch, "E876", {"start": v(2.4, 51.82) * mm, "end": v(3.05, 51.7) * mm});
            skLineSegment(sketch, "E877", {"start": v(3.05, 51.7) * mm, "end": v(3.71, 51.7) * mm});
            skLineSegment(sketch, "E878", {"start": v(3.71, 51.7) * mm, "end": v(4.35, 51.85) * mm});
            skLineSegment(sketch, "E879", {"start": v(4.35, 51.85) * mm, "end": v(4.8, 52.05) * mm});
            skLineSegment(sketch, "E880", {"start": v(4.8, 52.05) * mm, "end": v(4.94, 52.14) * mm});
            skLineSegment(sketch, "E881", {"start": v(4.94, 52.14) * mm, "end": v(5.07, 52.23) * mm});
            skLineSegment(sketch, "E882", {"start": v(5.07, 52.23) * mm, "end": v(5.44, 52.57) * mm});
            skLineSegment(sketch, "E883", {"start": v(5.44, 52.57) * mm, "end": v(5.83, 53.09) * mm});
            skLineSegment(sketch, "E884", {"start": v(5.83, 53.09) * mm, "end": v(6.1, 53.69) * mm});
            skLineSegment(sketch, "E885", {"start": v(6.1, 53.69) * mm, "end": v(6.24, 54.34) * mm});
            skLineSegment(sketch, "E886", {"start": v(6.24, 54.34) * mm, "end": v(6.26, 55.03) * mm});
            skLineSegment(sketch, "E887", {"start": v(6.26, 55.03) * mm, "end": v(6.15, 55.74) * mm});
            skLineSegment(sketch, "E888", {"start": v(6.15, 55.74) * mm, "end": v(5.91, 56.45) * mm});
            skLineSegment(sketch, "E889", {"start": v(5.91, 56.45) * mm, "end": v(5.65, 56.97) * mm});
            skLineSegment(sketch, "E890", {"start": v(5.65, 56.97) * mm, "end": v(5.54, 57.13) * mm});
            skLineSegment(sketch, "E891", {"start": v(5.54, 57.13) * mm, "end": v(5.44, 57.3) * mm});
            skLineSegment(sketch, "E892", {"start": v(5.44, 57.3) * mm, "end": v(5.06, 57.74) * mm});
            skLineSegment(sketch, "E893", {"start": v(5.06, 57.74) * mm, "end": v(4.5, 58.24) * mm});
            skLineSegment(sketch, "E894", {"start": v(4.5, 58.24) * mm, "end": v(3.9, 58.62) * mm});
            skLineSegment(sketch, "E895", {"start": v(3.9, 58.62) * mm, "end": v(3.25, 58.88) * mm});
            skLineSegment(sketch, "E896", {"start": v(3.25, 58.88) * mm, "end": v(2.59, 59) * mm});
            skLineSegment(sketch, "E897", {"start": v(2.59, 59) * mm, "end": v(1.93, 59) * mm});
            skLineSegment(sketch, "E898", {"start": v(1.93, 59) * mm, "end": v(1.3, 58.85) * mm});
            skLineSegment(sketch, "E899", {"start": v(1.3, 58.85) * mm, "end": v(0.84, 58.64) * mm});
            skLineSegment(sketch, "E900", {"start": v(0.84, 58.64) * mm, "end": v(0.7, 58.55) * mm});
            skLineSegment(sketch, "E901", {"start": v(-10.88, 56.76) * mm, "end": v(-10.81, 56.78) * mm});
            skLineSegment(sketch, "E902", {"start": v(-10.81, 56.78) * mm, "end": v(-10.6, 56.76) * mm});
            skLineSegment(sketch, "E903", {"start": v(-10.6, 56.76) * mm, "end": v(-10.4, 56.6) * mm});
            skLineSegment(sketch, "E904", {"start": v(-10.4, 56.6) * mm, "end": v(-10.23, 56.3) * mm});
            skLineSegment(sketch, "E905", {"start": v(-10.23, 56.3) * mm, "end": v(-10.13, 55.9) * mm});
            skLineSegment(sketch, "E906", {"start": v(-10.13, 55.9) * mm, "end": v(-10.07, 55.41) * mm});
            skLineSegment(sketch, "E907", {"start": v(-10.07, 55.41) * mm, "end": v(-10.06, 54.86) * mm});
            skLineSegment(sketch, "E908", {"start": v(-10.06, 54.86) * mm, "end": v(-10.1, 54.26) * mm});
            skLineSegment(sketch, "E909", {"start": v(-10.1, 54.26) * mm, "end": v(-10.16, 53.64) * mm});
            skLineSegment(sketch, "E910", {"start": v(-10.16, 53.64) * mm, "end": v(-10.26, 53.02) * mm});
            skLineSegment(sketch, "E911", {"start": v(-10.26, 53.02) * mm, "end": v(-10.4, 52.43) * mm});
            skLineSegment(sketch, "E912", {"start": v(-10.4, 52.43) * mm, "end": v(-10.56, 51.88) * mm});
            skLineSegment(sketch, "E913", {"start": v(-10.56, 51.88) * mm, "end": v(-10.74, 51.4) * mm});
            skLineSegment(sketch, "E914", {"start": v(-10.74, 51.4) * mm, "end": v(-10.95, 51.02) * mm});
            skLineSegment(sketch, "E915", {"start": v(-10.95, 51.02) * mm, "end": v(-11.17, 50.74) * mm});
            skLineSegment(sketch, "E916", {"start": v(-11.17, 50.74) * mm, "end": v(-11.4, 50.6) * mm});
            skLineSegment(sketch, "E917", {"start": v(-11.4, 50.6) * mm, "end": v(-11.6, 50.6) * mm});
            skLineSegment(sketch, "E918", {"start": v(-11.6, 50.6) * mm, "end": v(-11.65, 50.63) * mm});
            skLineSegment(sketch, "E919", {"start": v(-11.65, 50.63) * mm, "end": v(-11.72, 50.69) * mm});
            skLineSegment(sketch, "E920", {"start": v(-11.72, 50.69) * mm, "end": v(-11.91, 50.87) * mm});
            skLineSegment(sketch, "E921", {"start": v(-11.91, 50.87) * mm, "end": v(-12.15, 51.17) * mm});
            skLineSegment(sketch, "E922", {"start": v(-12.15, 51.17) * mm, "end": v(-12.35, 51.5) * mm});
            skLineSegment(sketch, "E923", {"start": v(-12.35, 51.5) * mm, "end": v(-12.52, 51.87) * mm});
            skLineSegment(sketch, "E924", {"start": v(-12.52, 51.87) * mm, "end": v(-12.66, 52.26) * mm});
            skLineSegment(sketch, "E925", {"start": v(-12.66, 52.26) * mm, "end": v(-12.76, 52.68) * mm});
            skLineSegment(sketch, "E926", {"start": v(-12.76, 52.68) * mm, "end": v(-12.81, 53.11) * mm});
            skLineSegment(sketch, "E927", {"start": v(-12.81, 53.11) * mm, "end": v(-12.82, 53.56) * mm});
            skLineSegment(sketch, "E928", {"start": v(-12.82, 53.56) * mm, "end": v(-12.78, 54) * mm});
            skLineSegment(sketch, "E929", {"start": v(-12.78, 54) * mm, "end": v(-12.69, 54.45) * mm});
            skLineSegment(sketch, "E930", {"start": v(-12.69, 54.45) * mm, "end": v(-12.54, 54.9) * mm});
            skLineSegment(sketch, "E931", {"start": v(-12.54, 54.9) * mm, "end": v(-12.34, 55.32) * mm});
            skLineSegment(sketch, "E932", {"start": v(-12.34, 55.32) * mm, "end": v(-12.07, 55.72) * mm});
            skLineSegment(sketch, "E933", {"start": v(-12.07, 55.72) * mm, "end": v(-11.74, 56.1) * mm});
            skLineSegment(sketch, "E934", {"start": v(-11.74, 56.1) * mm, "end": v(-11.35, 56.45) * mm});
            skLineSegment(sketch, "E935", {"start": v(-11.35, 56.45) * mm, "end": v(-11, 56.7) * mm});
            skLineSegment(sketch, "E936", {"start": v(-11, 56.7) * mm, "end": v(-10.88, 56.76) * mm});
            skLineSegment(sketch, "E937", {"start": v(7.9, 56.85) * mm, "end": v(7.83, 56.87) * mm});
            skLineSegment(sketch, "E938", {"start": v(7.83, 56.87) * mm, "end": v(7.62, 56.85) * mm});
            skLineSegment(sketch, "E939", {"start": v(7.62, 56.85) * mm, "end": v(7.4, 56.69) * mm});
            skLineSegment(sketch, "E940", {"start": v(7.4, 56.69) * mm, "end": v(7.25, 56.4) * mm});
            skLineSegment(sketch, "E941", {"start": v(7.25, 56.4) * mm, "end": v(7.14, 56) * mm});
            skLineSegment(sketch, "E942", {"start": v(7.14, 56) * mm, "end": v(7.09, 55.5) * mm});
            skLineSegment(sketch, "E943", {"start": v(7.09, 55.5) * mm, "end": v(7.07, 54.95) * mm});
            skLineSegment(sketch, "E944", {"start": v(7.07, 54.95) * mm, "end": v(7.1, 54.35) * mm});
            skLineSegment(sketch, "E945", {"start": v(7.1, 54.35) * mm, "end": v(7.17, 53.73) * mm});
            skLineSegment(sketch, "E946", {"start": v(7.17, 53.73) * mm, "end": v(7.28, 53.1) * mm});
            skLineSegment(sketch, "E947", {"start": v(7.28, 53.1) * mm, "end": v(7.41, 52.52) * mm});
            skLineSegment(sketch, "E948", {"start": v(7.41, 52.52) * mm, "end": v(7.57, 51.97) * mm});
            skLineSegment(sketch, "E949", {"start": v(7.57, 51.97) * mm, "end": v(7.76, 51.5) * mm});
            skLineSegment(sketch, "E950", {"start": v(7.76, 51.5) * mm, "end": v(7.96, 51.1) * mm});
            skLineSegment(sketch, "E951", {"start": v(7.96, 51.1) * mm, "end": v(8.19, 50.83) * mm});
            skLineSegment(sketch, "E952", {"start": v(8.19, 50.83) * mm, "end": v(8.42, 50.7) * mm});
            skLineSegment(sketch, "E953", {"start": v(8.42, 50.7) * mm, "end": v(8.61, 50.7) * mm});
            skLineSegment(sketch, "E954", {"start": v(8.61, 50.7) * mm, "end": v(8.66, 50.72) * mm});
            skLineSegment(sketch, "E955", {"start": v(8.66, 50.72) * mm, "end": v(8.73, 50.77) * mm});
            skLineSegment(sketch, "E956", {"start": v(8.73, 50.77) * mm, "end": v(8.93, 50.96) * mm});
            skLineSegment(sketch, "E957", {"start": v(8.93, 50.96) * mm, "end": v(9.16, 51.26) * mm});
            skLineSegment(sketch, "E958", {"start": v(9.16, 51.26) * mm, "end": v(9.36, 51.59) * mm});
            skLineSegment(sketch, "E959", {"start": v(9.36, 51.59) * mm, "end": v(9.54, 51.95) * mm});
            skLineSegment(sketch, "E960", {"start": v(9.54, 51.95) * mm, "end": v(9.67, 52.35) * mm});
            skLineSegment(sketch, "E961", {"start": v(9.67, 52.35) * mm, "end": v(9.77, 52.77) * mm});
            skLineSegment(sketch, "E962", {"start": v(9.77, 52.77) * mm, "end": v(9.82, 53.2) * mm});
            skLineSegment(sketch, "E963", {"start": v(9.82, 53.2) * mm, "end": v(9.83, 53.65) * mm});
            skLineSegment(sketch, "E964", {"start": v(9.83, 53.65) * mm, "end": v(9.8, 54.1) * mm});
            skLineSegment(sketch, "E965", {"start": v(9.8, 54.1) * mm, "end": v(9.7, 54.54) * mm});
            skLineSegment(sketch, "E966", {"start": v(9.7, 54.54) * mm, "end": v(9.56, 54.98) * mm});
            skLineSegment(sketch, "E967", {"start": v(9.56, 54.98) * mm, "end": v(9.35, 55.4) * mm});
            skLineSegment(sketch, "E968", {"start": v(9.35, 55.4) * mm, "end": v(9.09, 55.81) * mm});
            skLineSegment(sketch, "E969", {"start": v(9.09, 55.81) * mm, "end": v(8.76, 56.2) * mm});
            skLineSegment(sketch, "E970", {"start": v(8.76, 56.2) * mm, "end": v(8.36, 56.54) * mm});
            skLineSegment(sketch, "E971", {"start": v(8.36, 56.54) * mm, "end": v(8.01, 56.78) * mm});
            skLineSegment(sketch, "E972", {"start": v(8.01, 56.78) * mm, "end": v(7.9, 56.85) * mm});
            skLineSegment(sketch, "E973", {"start": v(2.37, 62.18) * mm, "end": v(2.63, 62.22) * mm});
            skLineSegment(sketch, "E974", {"start": v(2.63, 62.22) * mm, "end": v(3.4, 62.26) * mm});
            skLineSegment(sketch, "E975", {"start": v(3.4, 62.26) * mm, "end": v(4.36, 62.15) * mm});
            skLineSegment(sketch, "E976", {"start": v(4.36, 62.15) * mm, "end": v(5.23, 61.85) * mm});
            skLineSegment(sketch, "E977", {"start": v(5.23, 61.85) * mm, "end": v(5.98, 61.38) * mm});
            skLineSegment(sketch, "E978", {"start": v(5.98, 61.38) * mm, "end": v(6.6, 60.75) * mm});
            skLineSegment(sketch, "E979", {"start": v(6.6, 60.75) * mm, "end": v(7.06, 59.96) * mm});
            skLineSegment(sketch, "E980", {"start": v(7.06, 59.96) * mm, "end": v(7.34, 59.02) * mm});
            skLineSegment(sketch, "E981", {"start": v(7.34, 59.02) * mm, "end": v(7.42, 58.22) * mm});
            skLineSegment(sketch, "E982", {"start": v(7.42, 58.22) * mm, "end": v(7.41, 57.95) * mm});
            skLineSegment(sketch, "E983", {"start": v(7.41, 57.95) * mm, "end": v(7.41, 57.9) * mm});
            skLineSegment(sketch, "E984", {"start": v(7.41, 57.9) * mm, "end": v(7.33, 57.8) * mm});
            skLineSegment(sketch, "E985", {"start": v(7.33, 57.8) * mm, "end": v(7.13, 57.79) * mm});
            skLineSegment(sketch, "E986", {"start": v(7.13, 57.79) * mm, "end": v(6.83, 57.9) * mm});
            skLineSegment(sketch, "E987", {"start": v(6.83, 57.9) * mm, "end": v(6.44, 58.1) * mm});
            skLineSegment(sketch, "E988", {"start": v(6.44, 58.1) * mm, "end": v(6, 58.38) * mm});
            skLineSegment(sketch, "E989", {"start": v(6, 58.38) * mm, "end": v(5.5, 58.73) * mm});
            skLineSegment(sketch, "E990", {"start": v(5.5, 58.73) * mm, "end": v(5, 59.13) * mm});
            skLineSegment(sketch, "E991", {"start": v(5, 59.13) * mm, "end": v(4.47, 59.56) * mm});
            skLineSegment(sketch, "E992", {"start": v(4.47, 59.56) * mm, "end": v(3.97, 60) * mm});
            skLineSegment(sketch, "E993", {"start": v(3.97, 60) * mm, "end": v(3.5, 60.46) * mm});
            skLineSegment(sketch, "E994", {"start": v(3.5, 60.46) * mm, "end": v(3.07, 60.89) * mm});
            skLineSegment(sketch, "E995", {"start": v(3.07, 60.89) * mm, "end": v(2.71, 61.28) * mm});
            skLineSegment(sketch, "E996", {"start": v(2.71, 61.28) * mm, "end": v(2.45, 61.62) * mm});
            skLineSegment(sketch, "E997", {"start": v(2.45, 61.62) * mm, "end": v(2.29, 61.9) * mm});
            skLineSegment(sketch, "E998", {"start": v(2.29, 61.9) * mm, "end": v(2.26, 62.1) * mm});
            skLineSegment(sketch, "E999", {"start": v(2.26, 62.1) * mm, "end": v(2.34, 62.17) * mm});
            skLineSegment(sketch, "E1000", {"start": v(2.34, 62.17) * mm, "end": v(2.37, 62.18) * mm});
            skLineSegment(sketch, "E1001", {"start": v(-5.37, 62.27) * mm, "end": v(-5.62, 62.31) * mm});
            skLineSegment(sketch, "E1002", {"start": v(-5.62, 62.31) * mm, "end": v(-6.4, 62.35) * mm});
            skLineSegment(sketch, "E1003", {"start": v(-6.4, 62.35) * mm, "end": v(-7.35, 62.23) * mm});
            skLineSegment(sketch, "E1004", {"start": v(-7.35, 62.23) * mm, "end": v(-8.22, 61.94) * mm});
            skLineSegment(sketch, "E1005", {"start": v(-8.22, 61.94) * mm, "end": v(-8.98, 61.47) * mm});
            skLineSegment(sketch, "E1006", {"start": v(-8.98, 61.47) * mm, "end": v(-9.6, 60.84) * mm});
            skLineSegment(sketch, "E1007", {"start": v(-9.6, 60.84) * mm, "end": v(-10.06, 60.05) * mm});
            skLineSegment(sketch, "E1008", {"start": v(-10.06, 60.05) * mm, "end": v(-10.34, 59.11) * mm});
            skLineSegment(sketch, "E1009", {"start": v(-10.34, 59.11) * mm, "end": v(-10.42, 58.3) * mm});
            skLineSegment(sketch, "E1010", {"start": v(-10.42, 58.3) * mm, "end": v(-10.41, 58.04) * mm});
            skLineSegment(sketch, "E1011", {"start": v(-10.41, 58.04) * mm, "end": v(-10.4, 58) * mm});
            skLineSegment(sketch, "E1012", {"start": v(-10.4, 58) * mm, "end": v(-10.33, 57.9) * mm});
            skLineSegment(sketch, "E1013", {"start": v(-10.33, 57.9) * mm, "end": v(-10.13, 57.88) * mm});
            skLineSegment(sketch, "E1014", {"start": v(-10.13, 57.88) * mm, "end": v(-9.82, 57.98) * mm});
            skLineSegment(sketch, "E1015", {"start": v(-9.82, 57.98) * mm, "end": v(-9.44, 58.18) * mm});
            skLineSegment(sketch, "E1016", {"start": v(-9.44, 58.18) * mm, "end": v(-9, 58.47) * mm});
            skLineSegment(sketch, "E1017", {"start": v(-9, 58.47) * mm, "end": v(-8.5, 58.82) * mm});
            skLineSegment(sketch, "E1018", {"start": v(-8.5, 58.82) * mm, "end": v(-7.99, 59.22) * mm});
            skLineSegment(sketch, "E1019", {"start": v(-7.99, 59.22) * mm, "end": v(-7.47, 59.65) * mm});
            skLineSegment(sketch, "E1020", {"start": v(-7.47, 59.65) * mm, "end": v(-6.96, 60.1) * mm});
            skLineSegment(sketch, "E1021", {"start": v(-6.96, 60.1) * mm, "end": v(-6.49, 60.55) * mm});
            skLineSegment(sketch, "E1022", {"start": v(-6.49, 60.55) * mm, "end": v(-6.06, 60.98) * mm});
            skLineSegment(sketch, "E1023", {"start": v(-6.06, 60.98) * mm, "end": v(-5.7, 61.37) * mm});
            skLineSegment(sketch, "E1024", {"start": v(-5.7, 61.37) * mm, "end": v(-5.44, 61.71) * mm});
            skLineSegment(sketch, "E1025", {"start": v(-5.44, 61.71) * mm, "end": v(-5.29, 61.99) * mm});
            skLineSegment(sketch, "E1026", {"start": v(-5.29, 61.99) * mm, "end": v(-5.26, 62.18) * mm});
            skLineSegment(sketch, "E1027", {"start": v(-5.26, 62.18) * mm, "end": v(-5.34, 62.26) * mm});
            skLineSegment(sketch, "E1028", {"start": v(-5.34, 62.26) * mm, "end": v(-5.37, 62.27) * mm});
            skLineSegment(sketch, "E1029", {"start": v(-1.34, 62.98) * mm, "end": v(-1.5, 62.98) * mm});
            skLineSegment(sketch, "E1030", {"start": v(-1.5, 62.98) * mm, "end": v(-1.97, 62.93) * mm});
            skLineSegment(sketch, "E1031", {"start": v(-1.97, 62.93) * mm, "end": v(-2.56, 62.79) * mm});
            skLineSegment(sketch, "E1032", {"start": v(-2.56, 62.79) * mm, "end": v(-3.12, 62.56) * mm});
            skLineSegment(sketch, "E1033", {"start": v(-3.12, 62.56) * mm, "end": v(-3.61, 62.28) * mm});
            skLineSegment(sketch, "E1034", {"start": v(-3.61, 62.28) * mm, "end": v(-4.03, 61.96) * mm});
            skLineSegment(sketch, "E1035", {"start": v(-4.03, 61.96) * mm, "end": v(-4.35, 61.62) * mm});
            skLineSegment(sketch, "E1036", {"start": v(-4.35, 61.62) * mm, "end": v(-4.55, 61.3) * mm});
            skLineSegment(sketch, "E1037", {"start": v(-4.55, 61.3) * mm, "end": v(-4.63, 61.07) * mm});
            skLineSegment(sketch, "E1038", {"start": v(-4.63, 61.07) * mm, "end": v(-4.63, 61) * mm});
            skLineSegment(sketch, "E1039", {"start": v(-4.63, 61) * mm, "end": v(-4.63, 60.9) * mm});
            skLineSegment(sketch, "E1040", {"start": v(-4.63, 60.9) * mm, "end": v(-4.57, 60.65) * mm});
            skLineSegment(sketch, "E1041", {"start": v(-4.57, 60.65) * mm, "end": v(-4.4, 60.32) * mm});
            skLineSegment(sketch, "E1042", {"start": v(-4.4, 60.32) * mm, "end": v(-4.1, 60.01) * mm});
            skLineSegment(sketch, "E1043", {"start": v(-4.1, 60.01) * mm, "end": v(-3.72, 59.73) * mm});
            skLineSegment(sketch, "E1044", {"start": v(-3.72, 59.73) * mm, "end": v(-3.24, 59.5) * mm});
            skLineSegment(sketch, "E1045", {"start": v(-3.24, 59.5) * mm, "end": v(-2.68, 59.3) * mm});
            skLineSegment(sketch, "E1046", {"start": v(-2.68, 59.3) * mm, "end": v(-2.04, 59.18) * mm});
            skLineSegment(sketch, "E1047", {"start": v(-2.04, 59.18) * mm, "end": v(-1.51, 59.14) * mm});
            skLineSegment(sketch, "E1048", {"start": v(-1.51, 59.14) * mm, "end": v(-1.33, 59.13) * mm});
            skLineSegment(sketch, "E1049", {"start": v(-1.33, 59.13) * mm, "end": v(-1.15, 59.13) * mm});
            skLineSegment(sketch, "E1050", {"start": v(-1.15, 59.13) * mm, "end": v(-0.61, 59.16) * mm});
            skLineSegment(sketch, "E1051", {"start": v(-0.61, 59.16) * mm, "end": v(0.03, 59.26) * mm});
            skLineSegment(sketch, "E1052", {"start": v(0.03, 59.26) * mm, "end": v(0.6, 59.41) * mm});
            skLineSegment(sketch, "E1053", {"start": v(0.6, 59.41) * mm, "end": v(1.07, 59.62) * mm});
            skLineSegment(sketch, "E1054", {"start": v(1.07, 59.62) * mm, "end": v(1.45, 59.87) * mm});
            skLineSegment(sketch, "E1055", {"start": v(1.45, 59.87) * mm, "end": v(1.73, 60.15) * mm});
            skLineSegment(sketch, "E1056", {"start": v(1.73, 60.15) * mm, "end": v(1.9, 60.47) * mm});
            skLineSegment(sketch, "E1057", {"start": v(1.9, 60.47) * mm, "end": v(1.97, 60.73) * mm});
            skLineSegment(sketch, "E1058", {"start": v(1.97, 60.73) * mm, "end": v(1.97, 60.81) * mm});
            skLineSegment(sketch, "E1059", {"start": v(1.97, 60.81) * mm, "end": v(1.97, 60.91) * mm});
            skLineSegment(sketch, "E1060", {"start": v(1.97, 60.91) * mm, "end": v(1.9, 61.2) * mm});
            skLineSegment(sketch, "E1061", {"start": v(1.9, 61.2) * mm, "end": v(1.66, 61.6) * mm});
            skLineSegment(sketch, "E1062", {"start": v(1.66, 61.6) * mm, "end": v(1.32, 61.97) * mm});
            skLineSegment(sketch, "E1063", {"start": v(1.32, 61.97) * mm, "end": v(0.87, 62.3) * mm});
            skLineSegment(sketch, "E1064", {"start": v(0.87, 62.3) * mm, "end": v(0.36, 62.58) * mm});
            skLineSegment(sketch, "E1065", {"start": v(0.36, 62.58) * mm, "end": v(-0.2, 62.8) * mm});
            skLineSegment(sketch, "E1066", {"start": v(-0.2, 62.8) * mm, "end": v(-0.78, 62.93) * mm});
            skLineSegment(sketch, "E1067", {"start": v(-0.78, 62.93) * mm, "end": v(-1.2, 62.98) * mm});
            skLineSegment(sketch, "E1068", {"start": v(-1.2, 62.98) * mm, "end": v(-1.34, 62.98) * mm});
            skLineSegment(sketch, "E1069", {"start": v(-1.24, 44.4) * mm, "end": v(-1.1, 44.41) * mm});
            skLineSegment(sketch, "E1070", {"start": v(-1.1, 44.41) * mm, "end": v(-0.68, 44.4) * mm});
            skLineSegment(sketch, "E1071", {"start": v(-0.68, 44.4) * mm, "end": v(-0.1, 44.35) * mm});
            skLineSegment(sketch, "E1072", {"start": v(-0.1, 44.35) * mm, "end": v(0.48, 44.25) * mm});
            skLineSegment(sketch, "E1073", {"start": v(0.48, 44.25) * mm, "end": v(1.01, 44.1) * mm});
            skLineSegment(sketch, "E1074", {"start": v(1.01, 44.1) * mm, "end": v(1.48, 43.93) * mm});
            skLineSegment(sketch, "E1075", {"start": v(1.48, 43.93) * mm, "end": v(1.85, 43.72) * mm});
            skLineSegment(sketch, "E1076", {"start": v(1.85, 43.72) * mm, "end": v(2.09, 43.48) * mm});
            skLineSegment(sketch, "E1077", {"start": v(2.09, 43.48) * mm, "end": v(2.18, 43.3) * mm});
            skLineSegment(sketch, "E1078", {"start": v(2.18, 43.3) * mm, "end": v(2.18, 43.23) * mm});
            skLineSegment(sketch, "E1079", {"start": v(2.18, 43.23) * mm, "end": v(2.18, 43.15) * mm});
            skLineSegment(sketch, "E1080", {"start": v(2.18, 43.15) * mm, "end": v(2.1, 42.93) * mm});
            skLineSegment(sketch, "E1081", {"start": v(2.1, 42.93) * mm, "end": v(1.88, 42.59) * mm});
            skLineSegment(sketch, "E1082", {"start": v(1.88, 42.59) * mm, "end": v(1.53, 42.22) * mm});
            skLineSegment(sketch, "E1083", {"start": v(1.53, 42.22) * mm, "end": v(1.08, 41.85) * mm});
            skLineSegment(sketch, "E1084", {"start": v(1.08, 41.85) * mm, "end": v(0.54, 41.52) * mm});
            skLineSegment(sketch, "E1085", {"start": v(0.54, 41.52) * mm, "end": v(-0.05, 41.25) * mm});
            skLineSegment(sketch, "E1086", {"start": v(-0.05, 41.25) * mm, "end": v(-0.69, 41.08) * mm});
            skLineSegment(sketch, "E1087", {"start": v(-0.69, 41.08) * mm, "end": v(-1.18, 41.01) * mm});
            skLineSegment(sketch, "E1088", {"start": v(-1.18, 41.01) * mm, "end": v(-1.34, 41.02) * mm});
            skLineSegment(sketch, "E1089", {"start": v(-1.34, 41.02) * mm, "end": v(-1.5, 41.01) * mm});
            skLineSegment(sketch, "E1090", {"start": v(-1.5, 41.01) * mm, "end": v(-2.01, 41.06) * mm});
            skLineSegment(sketch, "E1091", {"start": v(-2.01, 41.06) * mm, "end": v(-2.66, 41.22) * mm});
            skLineSegment(sketch, "E1092", {"start": v(-2.66, 41.22) * mm, "end": v(-3.26, 41.48) * mm});
            skLineSegment(sketch, "E1093", {"start": v(-3.26, 41.48) * mm, "end": v(-3.8, 41.8) * mm});
            skLineSegment(sketch, "E1094", {"start": v(-3.8, 41.8) * mm, "end": v(-4.25, 42.14) * mm});
            skLineSegment(sketch, "E1095", {"start": v(-4.25, 42.14) * mm, "end": v(-4.6, 42.48) * mm});
            skLineSegment(sketch, "E1096", {"start": v(-4.6, 42.48) * mm, "end": v(-4.82, 42.79) * mm});
            skLineSegment(sketch, "E1097", {"start": v(-4.82, 42.79) * mm, "end": v(-4.89, 42.97) * mm});
            skLineSegment(sketch, "E1098", {"start": v(-4.89, 42.97) * mm, "end": v(-4.89, 43.03) * mm});
            skLineSegment(sketch, "E1099", {"start": v(-4.89, 43.03) * mm, "end": v(-4.89, 43.1) * mm});
            skLineSegment(sketch, "E1100", {"start": v(-4.89, 43.1) * mm, "end": v(-4.8, 43.32) * mm});
            skLineSegment(sketch, "E1101", {"start": v(-4.8, 43.32) * mm, "end": v(-4.53, 43.59) * mm});
            skLineSegment(sketch, "E1102", {"start": v(-4.53, 43.59) * mm, "end": v(-4.13, 43.82) * mm});
            skLineSegment(sketch, "E1103", {"start": v(-4.13, 43.82) * mm, "end": v(-3.62, 44.03) * mm});
            skLineSegment(sketch, "E1104", {"start": v(-3.62, 44.03) * mm, "end": v(-3.04, 44.2) * mm});
            skLineSegment(sketch, "E1105", {"start": v(-3.04, 44.2) * mm, "end": v(-2.43, 44.32) * mm});
            skLineSegment(sketch, "E1106", {"start": v(-2.43, 44.32) * mm, "end": v(-1.82, 44.39) * mm});
            skLineSegment(sketch, "E1107", {"start": v(-1.82, 44.39) * mm, "end": v(-1.39, 44.4) * mm});
            skLineSegment(sketch, "E1108", {"start": v(-1.39, 44.4) * mm, "end": v(-1.24, 44.4) * mm});
            skLineSegment(sketch, "E1109", {"start": v(-6.63, 48.6) * mm, "end": v(-6.53, 48.48) * mm});
            skLineSegment(sketch, "E1110", {"start": v(-6.53, 48.48) * mm, "end": v(-6.27, 48.1) * mm});
            skLineSegment(sketch, "E1111", {"start": v(-6.27, 48.1) * mm, "end": v(-5.97, 47.52) * mm});
            skLineSegment(sketch, "E1112", {"start": v(-5.97, 47.52) * mm, "end": v(-5.74, 46.92) * mm});
            skLineSegment(sketch, "E1113", {"start": v(-5.74, 46.92) * mm, "end": v(-5.6, 46.32) * mm});
            skLineSegment(sketch, "E1114", {"start": v(-5.6, 46.32) * mm, "end": v(-5.53, 45.75) * mm});
            skLineSegment(sketch, "E1115", {"start": v(-5.53, 45.75) * mm, "end": v(-5.57, 45.24) * mm});
            skLineSegment(sketch, "E1116", {"start": v(-5.57, 45.24) * mm, "end": v(-5.72, 44.81) * mm});
            skLineSegment(sketch, "E1117", {"start": v(-5.72, 44.81) * mm, "end": v(-5.9, 44.56) * mm});
            skLineSegment(sketch, "E1118", {"start": v(-5.9, 44.56) * mm, "end": v(-5.98, 44.5) * mm});
            skLineSegment(sketch, "E1119", {"start": v(-5.98, 44.5) * mm, "end": v(-6.07, 44.45) * mm});
            skLineSegment(sketch, "E1120", {"start": v(-6.07, 44.45) * mm, "end": v(-6.34, 44.35) * mm});
            skLineSegment(sketch, "E1121", {"start": v(-6.34, 44.35) * mm, "end": v(-6.8, 44.28) * mm});
            skLineSegment(sketch, "E1122", {"start": v(-6.8, 44.28) * mm, "end": v(-7.3, 44.3) * mm});
            skLineSegment(sketch, "E1123", {"start": v(-7.3, 44.3) * mm, "end": v(-7.87, 44.43) * mm});
            skLineSegment(sketch, "E1124", {"start": v(-7.87, 44.43) * mm, "end": v(-8.47, 44.67) * mm});
            skLineSegment(sketch, "E1125", {"start": v(-8.47, 44.67) * mm, "end": v(-9.07, 45.04) * mm});
            skLineSegment(sketch, "E1126", {"start": v(-9.07, 45.04) * mm, "end": v(-9.66, 45.57) * mm});
            skLineSegment(sketch, "E1127", {"start": v(-9.66, 45.57) * mm, "end": v(-10.09, 46.06) * mm});
            skLineSegment(sketch, "E1128", {"start": v(-10.09, 46.06) * mm, "end": v(-10.21, 46.24) * mm});
            skLineSegment(sketch, "E1129", {"start": v(-10.21, 46.24) * mm, "end": v(-10.3, 46.4) * mm});
            skLineSegment(sketch, "E1130", {"start": v(-10.3, 46.4) * mm, "end": v(-10.52, 46.88) * mm});
            skLineSegment(sketch, "E1131", {"start": v(-10.52, 46.88) * mm, "end": v(-10.73, 47.5) * mm});
            skLineSegment(sketch, "E1132", {"start": v(-10.73, 47.5) * mm, "end": v(-10.86, 48.1) * mm});
            skLineSegment(sketch, "E1133", {"start": v(-10.86, 48.1) * mm, "end": v(-10.9, 48.67) * mm});
            skLineSegment(sketch, "E1134", {"start": v(-10.9, 48.67) * mm, "end": v(-10.87, 49.17) * mm});
            skLineSegment(sketch, "E1135", {"start": v(-10.87, 49.17) * mm, "end": v(-10.76, 49.6) * mm});
            skLineSegment(sketch, "E1136", {"start": v(-10.76, 49.6) * mm, "end": v(-10.6, 49.95) * mm});
            skLineSegment(sketch, "E1137", {"start": v(-10.6, 49.95) * mm, "end": v(-10.44, 50.15) * mm});
            skLineSegment(sketch, "E1138", {"start": v(-10.44, 50.15) * mm, "end": v(-10.37, 50.2) * mm});
            skLineSegment(sketch, "E1139", {"start": v(-10.37, 50.2) * mm, "end": v(-10.28, 50.25) * mm});
            skLineSegment(sketch, "E1140", {"start": v(-10.28, 50.25) * mm, "end": v(-9.97, 50.36) * mm});
            skLineSegment(sketch, "E1141", {"start": v(-9.97, 50.36) * mm, "end": v(-9.53, 50.4) * mm});
            skLineSegment(sketch, "E1142", {"start": v(-9.53, 50.4) * mm, "end": v(-9.06, 50.32) * mm});
            skLineSegment(sketch, "E1143", {"start": v(-9.06, 50.32) * mm, "end": v(-8.57, 50.14) * mm});
            skLineSegment(sketch, "E1144", {"start": v(-8.57, 50.14) * mm, "end": v(-8.07, 49.87) * mm});
            skLineSegment(sketch, "E1145", {"start": v(-8.07, 49.87) * mm, "end": v(-7.58, 49.52) * mm});
            skLineSegment(sketch, "E1146", {"start": v(-7.58, 49.52) * mm, "end": v(-7.1, 49.09) * mm});
            skLineSegment(sketch, "E1147", {"start": v(-7.1, 49.09) * mm, "end": v(-6.74, 48.73) * mm});
            skLineSegment(sketch, "E1148", {"start": v(-6.74, 48.73) * mm, "end": v(-6.63, 48.6) * mm});
            skLineSegment(sketch, "E1149", {"start": v(3.94, 49) * mm, "end": v(3.83, 48.87) * mm});
            skLineSegment(sketch, "E1150", {"start": v(3.83, 48.87) * mm, "end": v(3.54, 48.46) * mm});
            skLineSegment(sketch, "E1151", {"start": v(3.54, 48.46) * mm, "end": v(3.2, 47.85) * mm});
            skLineSegment(sketch, "E1152", {"start": v(3.2, 47.85) * mm, "end": v(2.93, 47.2) * mm});
            skLineSegment(sketch, "E1153", {"start": v(2.93, 47.2) * mm, "end": v(2.74, 46.55) * mm});
            skLineSegment(sketch, "E1154", {"start": v(2.74, 46.55) * mm, "end": v(2.65, 45.92) * mm});
            skLineSegment(sketch, "E1155", {"start": v(2.65, 45.92) * mm, "end": v(2.65, 45.35) * mm});
            skLineSegment(sketch, "E1156", {"start": v(2.65, 45.35) * mm, "end": v(2.77, 44.87) * mm});
            skLineSegment(sketch, "E1157", {"start": v(2.77, 44.87) * mm, "end": v(2.93, 44.58) * mm});
            skLineSegment(sketch, "E1158", {"start": v(2.93, 44.58) * mm, "end": v(3, 44.5) * mm});
            skLineSegment(sketch, "E1159", {"start": v(3, 44.5) * mm, "end": v(3.09, 44.45) * mm});
            skLineSegment(sketch, "E1160", {"start": v(3.09, 44.45) * mm, "end": v(3.36, 44.32) * mm});
            skLineSegment(sketch, "E1161", {"start": v(3.36, 44.32) * mm, "end": v(3.81, 44.2) * mm});
            skLineSegment(sketch, "E1162", {"start": v(3.81, 44.2) * mm, "end": v(4.35, 44.2) * mm});
            skLineSegment(sketch, "E1163", {"start": v(4.35, 44.2) * mm, "end": v(4.94, 44.3) * mm});
            skLineSegment(sketch, "E1164", {"start": v(4.94, 44.3) * mm, "end": v(5.57, 44.52) * mm});
            skLineSegment(sketch, "E1165", {"start": v(5.57, 44.52) * mm, "end": v(6.2, 44.9) * mm});
            skLineSegment(sketch, "E1166", {"start": v(6.2, 44.9) * mm, "end": v(6.84, 45.43) * mm});
            skLineSegment(sketch, "E1167", {"start": v(6.84, 45.43) * mm, "end": v(7.31, 45.96) * mm});
            skLineSegment(sketch, "E1168", {"start": v(7.31, 45.96) * mm, "end": v(7.45, 46.15) * mm});
            skLineSegment(sketch, "E1169", {"start": v(7.45, 46.15) * mm, "end": v(7.55, 46.28) * mm});
            skLineSegment(sketch, "E1170", {"start": v(7.55, 46.28) * mm, "end": v(7.8, 46.73) * mm});
            skLineSegment(sketch, "E1171", {"start": v(7.8, 46.73) * mm, "end": v(8.03, 47.37) * mm});
            skLineSegment(sketch, "E1172", {"start": v(8.03, 47.37) * mm, "end": v(8.15, 48.04) * mm});
            skLineSegment(sketch, "E1173", {"start": v(8.15, 48.04) * mm, "end": v(8.17, 48.7) * mm});
            skLineSegment(sketch, "E1174", {"start": v(8.17, 48.7) * mm, "end": v(8.1, 49.33) * mm});
            skLineSegment(sketch, "E1175", {"start": v(8.1, 49.33) * mm, "end": v(7.97, 49.88) * mm});
            skLineSegment(sketch, "E1176", {"start": v(7.97, 49.88) * mm, "end": v(7.78, 50.34) * mm});
            skLineSegment(sketch, "E1177", {"start": v(7.78, 50.34) * mm, "end": v(7.62, 50.59) * mm});
            skLineSegment(sketch, "E1178", {"start": v(7.62, 50.59) * mm, "end": v(7.55, 50.65) * mm});
            skLineSegment(sketch, "E1179", {"start": v(7.55, 50.65) * mm, "end": v(7.47, 50.72) * mm});
            skLineSegment(sketch, "E1180", {"start": v(7.47, 50.72) * mm, "end": v(7.18, 50.86) * mm});
            skLineSegment(sketch, "E1181", {"start": v(7.18, 50.86) * mm, "end": v(6.77, 50.91) * mm});
            skLineSegment(sketch, "E1182", {"start": v(6.77, 50.91) * mm, "end": v(6.33, 50.84) * mm});
            skLineSegment(sketch, "E1183", {"start": v(6.33, 50.84) * mm, "end": v(5.87, 50.65) * mm});
            skLineSegment(sketch, "E1184", {"start": v(5.87, 50.65) * mm, "end": v(5.4, 50.35) * mm});
            skLineSegment(sketch, "E1185", {"start": v(5.4, 50.35) * mm, "end": v(4.91, 49.97) * mm});
            skLineSegment(sketch, "E1186", {"start": v(4.91, 49.97) * mm, "end": v(4.42, 49.51) * mm});
            skLineSegment(sketch, "E1187", {"start": v(4.42, 49.51) * mm, "end": v(4.05, 49.13) * mm});
            skLineSegment(sketch, "E1188", {"start": v(4.05, 49.13) * mm, "end": v(3.94, 49) * mm});
            skLineSegment(sketch, "E1189", {"start": v(3.94, 49) * mm, "end": v(3.94, 49) * mm});
            const initialGuessF8  = {"E80": [-0.03543, 0.1096, 1, 0, 0.00608], "E81": [-0.02543, 0.0984, 1, 0, 0.00798], "E82": [-0.00043, 0.09261, 1, 0, 0.00237]};
            skSetInitialGuess(sketch, initialGuessF8);
            skSolve(sketch);
        }
        {
            var Q0;
            Q0=makeQuery(id+"F8.imprint","IMPRINT",FACE,{"disambiguationData":[TD([[makeQuery(id+"F8.imprint","IMPRINT",EDGE,{"derivedFrom":sQuery(id+"F8.wireOp",EDGE,"E77.bottom")}),1.0]])]});
            extrude(context, id + "F9", {"entities" : qUnion([Q0]), "operationType" : NewBodyOperationType.REMOVE, "oppositeDirection" : true, "depth" : 2 * mm, "offsetDistance" : 25 * mm});
        }
        {
            var Q0;
            Q0 = qSketchRegion(id + "F8", true);
            extrude(context, id + "F10", {"entities" : qUnion([Q0]), "operationType" : NewBodyOperationType.REMOVE, "oppositeDirection" : true, "depth" : .2 * mm, "offsetDistance" : 25 * mm});
        }
    });